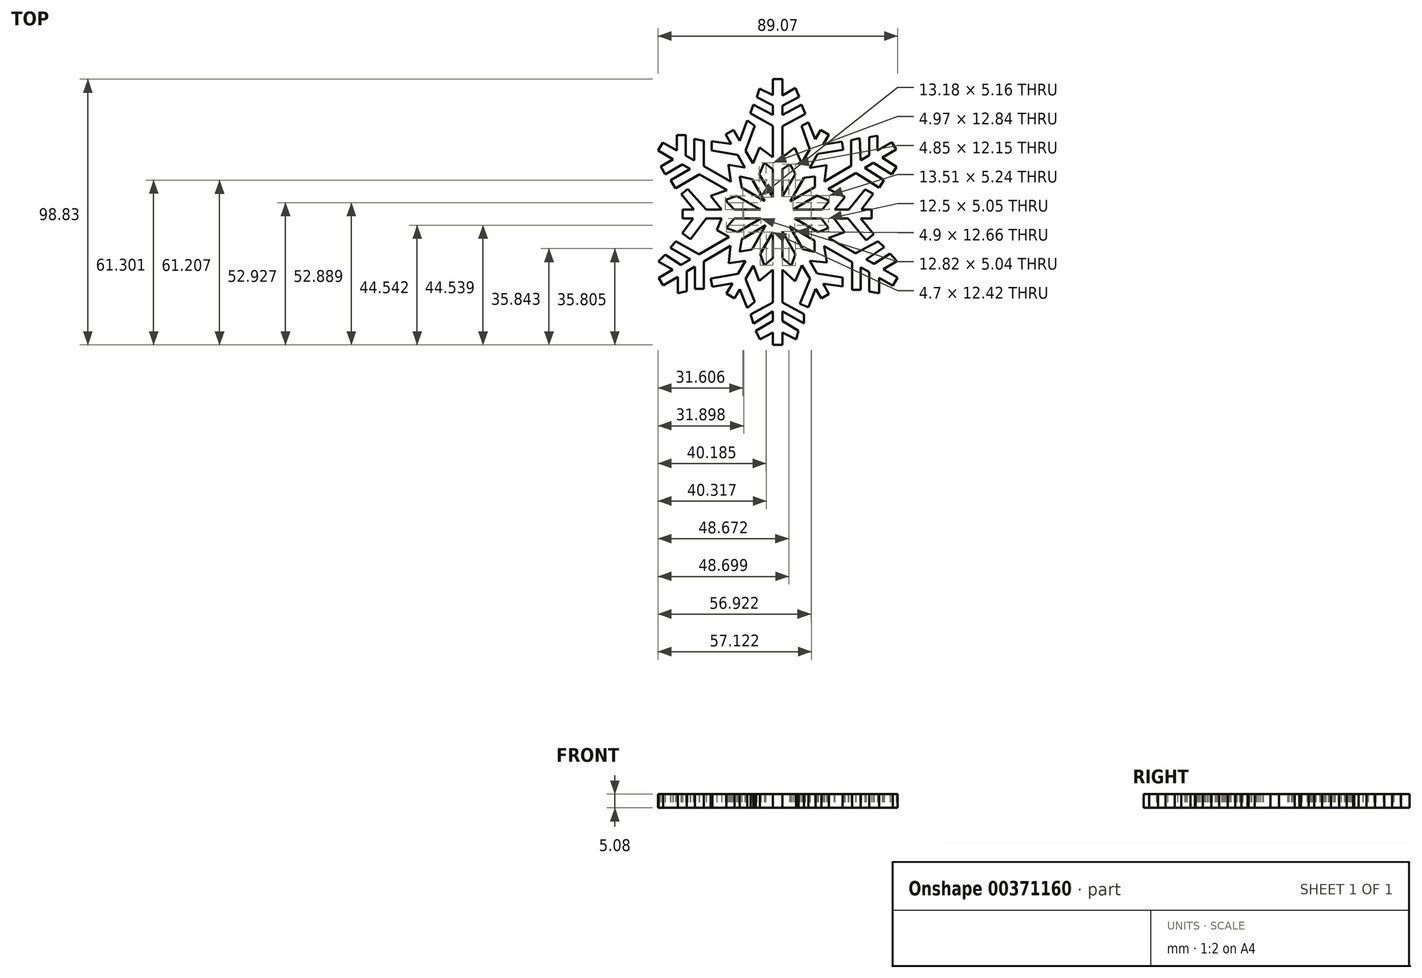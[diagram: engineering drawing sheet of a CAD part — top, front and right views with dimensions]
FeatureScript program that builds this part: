
annotation { "Feature Type Name" : "Feature", "Feature Type Description" : "" }
export const myFeature = defineFeature(function(context is Context, id is Id, definition is map)
    precondition{}
    {
        {
            var Q0;
            Q0=qCreatedBy(makeId("Top.planeOp"),FACE);
            var sketch = newSketch(context, id + "F0", { "sketchPlane" : qUnion([Q0])});
            skLineSegment(sketch, "E0.bottom", {"start": v(-35.17, -1.59) * mm, "end": v(35.1, -1.59) * mm});
            skLineSegment(sketch, "E0.top", {"start": v(-35.17, 1.66) * mm, "end": v(35.1, 1.66) * mm});
            skLineSegment(sketch, "E0.left", {"start": v(-35.17, -1.59) * mm, "end": v(-35.17, 1.66) * mm});
            skLineSegment(sketch, "E0.right", {"start": v(35.1, -1.59) * mm, "end": v(35.1, 1.66) * mm});
            skLineSegment(sketch, "E1", {"start": v(-19.17, 29.64) * mm, "end": v(-16.28, 31.23) * mm});
            skLineSegment(sketch, "E2", {"start": v(-16.28, 31.23) * mm, "end": v(19.17, -29.65) * mm});
            skLineSegment(sketch, "E3", {"start": v(19.17, -29.65) * mm, "end": v(16.32, -31.31) * mm});
            skLineSegment(sketch, "E4", {"start": v(16.32, -31.31) * mm, "end": v(-19.17, 29.64) * mm});
            skLineSegment(sketch, "E5", {"start": v(-42.5, 26.63) * mm, "end": v(-44.39, 23.66) * mm});
            skLineSegment(sketch, "E6", {"start": v(-44.39, 23.66) * mm, "end": v(42.93, -26.64) * mm});
            skLineSegment(sketch, "E7", {"start": v(42.93, -26.64) * mm, "end": v(44.68, -23.6) * mm});
            skLineSegment(sketch, "E8", {"start": v(44.68, -23.6) * mm, "end": v(-42.5, 26.63) * mm});
            skLineSegment(sketch, "E9", {"start": v(16.12, 31.24) * mm, "end": v(19.1, 29.52) * mm});
            skLineSegment(sketch, "E10", {"start": v(19.1, 29.52) * mm, "end": v(-15.92, -31.28) * mm});
            skLineSegment(sketch, "E11", {"start": v(-15.92, -31.28) * mm, "end": v(-18.9, -29.56) * mm});
            skLineSegment(sketch, "E12", {"start": v(-18.9, -29.56) * mm, "end": v(16.12, 31.24) * mm});
            skLineSegment(sketch, "E13", {"start": v(42.56, 26.73) * mm, "end": v(44.15, 24) * mm});
            skLineSegment(sketch, "E14", {"start": v(44.15, 24) * mm, "end": v(-42.48, -26.44) * mm});
            skLineSegment(sketch, "E15", {"start": v(-42.48, -26.44) * mm, "end": v(-44.07, -23.7) * mm});
            skLineSegment(sketch, "E16", {"start": v(-44.07, -23.7) * mm, "end": v(42.56, 26.73) * mm});
            skLineSegment(sketch, "E17", {"start": v(-7.62, 43.46) * mm, "end": v(-6.6, 46.62) * mm});
            skLineSegment(sketch, "E18", {"start": v(-10.07, 37.55) * mm, "end": v(-8.85, 40.7) * mm});
            skLineSegment(sketch, "E19", {"start": v(1.86, 44.07) * mm, "end": v(6.75, 46.93) * mm});
            skLineSegment(sketch, "E20", {"start": v(6.75, 46.93) * mm, "end": v(8.18, 43.67) * mm});
            skLineSegment(sketch, "E21", {"start": v(8.18, 43.67) * mm, "end": v(1.86, 40.34) * mm});
            skLineSegment(sketch, "E22", {"start": v(1.86, 36.85) * mm, "end": v(9, 40.7) * mm});
            skLineSegment(sketch, "E23", {"start": v(9, 40.7) * mm, "end": v(10.42, 37.24) * mm});
            skLineSegment(sketch, "E24", {"start": v(10.42, 37.24) * mm, "end": v(1.86, 32.7) * mm});
            skLineSegment(sketch, "E25", {"start": v(12.01, 24.1) * mm, "end": v(9.05, 32.76) * mm});
            skLineSegment(sketch, "E26", {"start": v(9.05, 32.76) * mm, "end": v(11.56, 34.1) * mm});
            skLineSegment(sketch, "E27", {"start": v(11.56, 34.1) * mm, "end": v(14.14, 27.8) * mm});
            skLineSegment(sketch, "E28", {"start": v(17, 25.85) * mm, "end": v(24, 26.9) * mm});
            skLineSegment(sketch, "E29", {"start": v(24, 26.9) * mm, "end": v(24.46, 23.86) * mm});
            skLineSegment(sketch, "E30", {"start": v(24.46, 23.86) * mm, "end": v(15.03, 22.43) * mm});
            skLineSegment(sketch, "E31", {"start": v(34.16, 21.85) * mm, "end": v(34.16, 28.6) * mm});
            skLineSegment(sketch, "E32", {"start": v(34.16, 28.6) * mm, "end": v(37.18, 29.12) * mm});
            skLineSegment(sketch, "E33", {"start": v(37.18, 29.12) * mm, "end": v(37.18, 23.6) * mm});
            skLineSegment(sketch, "E34", {"start": v(38.95, 20.98) * mm, "end": v(44.32, 17.6) * mm});
            skLineSegment(sketch, "E35", {"start": v(44.32, 17.6) * mm, "end": v(42.52, 14.74) * mm});
            skLineSegment(sketch, "E36", {"start": v(42.52, 14.74) * mm, "end": v(35.65, 19.05) * mm});
            skLineSegment(sketch, "E37", {"start": v(32.55, 17.25) * mm, "end": v(39.66, 12.67) * mm});
            skLineSegment(sketch, "E38", {"start": v(39.66, 12.67) * mm, "end": v(37.8, 9.8) * mm});
            skLineSegment(sketch, "E39", {"start": v(37.8, 9.8) * mm, "end": v(29.23, 15.32) * mm});
            skLineSegment(sketch, "E40", {"start": v(27.4, 17.91) * mm, "end": v(27.4, 27.47) * mm});
            skLineSegment(sketch, "E41", {"start": v(27.4, 27.47) * mm, "end": v(30.54, 28.26) * mm});
            skLineSegment(sketch, "E42", {"start": v(30.54, 28.26) * mm, "end": v(31, 20) * mm});
            skLineSegment(sketch, "E43", {"start": v(26.57, 1.66) * mm, "end": v(32.65, 9.23) * mm});
            skLineSegment(sketch, "E44", {"start": v(32.65, 9.23) * mm, "end": v(35.7, 7.51) * mm});
            skLineSegment(sketch, "E45", {"start": v(35.7, 7.51) * mm, "end": v(31.2, 1.66) * mm});
            skLineSegment(sketch, "E46", {"start": v(30.93, -1.59) * mm, "end": v(35.82, -7.43) * mm});
            skLineSegment(sketch, "E47", {"start": v(35.82, -7.43) * mm, "end": v(33.06, -9.74) * mm});
            skLineSegment(sketch, "E48", {"start": v(33.06, -9.74) * mm, "end": v(26.23, -1.59) * mm});
            skLineSegment(sketch, "E49", {"start": v(29.1, -14.62) * mm, "end": v(37.4, -10.07) * mm});
            skLineSegment(sketch, "E50", {"start": v(37.4, -10.07) * mm, "end": v(39.79, -12.32) * mm});
            skLineSegment(sketch, "E51", {"start": v(39.79, -12.32) * mm, "end": v(33.05, -16.9) * mm});
            skLineSegment(sketch, "E52", {"start": v(35.88, -18.52) * mm, "end": v(41.9, -14.7) * mm});
            skLineSegment(sketch, "E53", {"start": v(41.9, -14.7) * mm, "end": v(44.41, -17.47) * mm});
            skLineSegment(sketch, "E54", {"start": v(44.41, -17.47) * mm, "end": v(39.42, -20.56) * mm});
            skLineSegment(sketch, "E55", {"start": v(37.86, -23.72) * mm, "end": v(37.86, -29.37) * mm});
            skLineSegment(sketch, "E56", {"start": v(37.86, -29.37) * mm, "end": v(34.1, -28.84) * mm});
            skLineSegment(sketch, "E57", {"start": v(34.1, -28.84) * mm, "end": v(34.1, -21.56) * mm});
            skLineSegment(sketch, "E58", {"start": v(30.93, -19.73) * mm, "end": v(30.93, -28.18) * mm});
            skLineSegment(sketch, "E59", {"start": v(30.93, -28.18) * mm, "end": v(27.76, -28.18) * mm});
            skLineSegment(sketch, "E60", {"start": v(27.76, -28.18) * mm, "end": v(27.76, -17.9) * mm});
            skLineSegment(sketch, "E61", {"start": v(14.72, -22.01) * mm, "end": v(24.2, -23.55) * mm});
            skLineSegment(sketch, "E62", {"start": v(24.2, -23.55) * mm, "end": v(24.2, -26.86) * mm});
            skLineSegment(sketch, "E63", {"start": v(24.2, -26.86) * mm, "end": v(16.98, -25.9) * mm});
            skLineSegment(sketch, "E64", {"start": v(14.26, -27.79) * mm, "end": v(11.5, -34.65) * mm});
            skLineSegment(sketch, "E65", {"start": v(11.5, -34.65) * mm, "end": v(8.38, -33.4) * mm});
            skLineSegment(sketch, "E66", {"start": v(8.38, -33.4) * mm, "end": v(12.12, -24.1) * mm});
            skLineSegment(sketch, "E67", {"start": v(1.86, -32.89) * mm, "end": v(9.94, -37.17) * mm});
            skLineSegment(sketch, "E68", {"start": v(9.94, -37.17) * mm, "end": v(9.94, -40.6) * mm});
            skLineSegment(sketch, "E69", {"start": v(9.94, -40.6) * mm, "end": v(1.86, -36.14) * mm});
            skLineSegment(sketch, "E70", {"start": v(1.86, -39.74) * mm, "end": v(7.89, -43.34) * mm});
            skLineSegment(sketch, "E71", {"start": v(7.89, -43.34) * mm, "end": v(7.03, -46.6) * mm});
            skLineSegment(sketch, "E72", {"start": v(7.03, -46.6) * mm, "end": v(1.86, -44.03) * mm});
            skLineSegment(sketch, "E73", {"start": v(-8.06, -43.34) * mm, "end": v(-6.43, -46.56) * mm});
            skLineSegment(sketch, "E74", {"start": v(-9.94, -37.34) * mm, "end": v(-8.91, -40.77) * mm});
            skLineSegment(sketch, "E75", {"start": v(-11.77, -24.08) * mm, "end": v(-8.4, -32.54) * mm});
            skLineSegment(sketch, "E76", {"start": v(-8.4, -32.54) * mm, "end": v(-11.14, -34.94) * mm});
            skLineSegment(sketch, "E77", {"start": v(-11.14, -34.94) * mm, "end": v(-13.95, -27.85) * mm});
            skLineSegment(sketch, "E78", {"start": v(-16.68, -25.69) * mm, "end": v(-24.17, -27.06) * mm});
            skLineSegment(sketch, "E79", {"start": v(-24.17, -27.06) * mm, "end": v(-24.73, -24.01) * mm});
            skLineSegment(sketch, "E80", {"start": v(-24.73, -24.01) * mm, "end": v(-14.65, -22.17) * mm});
            skLineSegment(sketch, "E81", {"start": v(-27.35, -17.63) * mm, "end": v(-27.35, -27.74) * mm});
            skLineSegment(sketch, "E82", {"start": v(-27.35, -27.74) * mm, "end": v(-30.68, -27.74) * mm});
            skLineSegment(sketch, "E83", {"start": v(-30.68, -27.74) * mm, "end": v(-30.68, -19.57) * mm});
            skLineSegment(sketch, "E84", {"start": v(-33.66, -21.3) * mm, "end": v(-33.66, -28.6) * mm});
            skLineSegment(sketch, "E85", {"start": v(-33.66, -28.6) * mm, "end": v(-37.03, -29.46) * mm});
            skLineSegment(sketch, "E86", {"start": v(-37.03, -29.46) * mm, "end": v(-37.03, -23.26) * mm});
            skLineSegment(sketch, "E87", {"start": v(-38.9, -20.7) * mm, "end": v(-44.23, -17.63) * mm});
            skLineSegment(sketch, "E88", {"start": v(-44.23, -17.63) * mm, "end": v(-41.65, -15.06) * mm});
            skLineSegment(sketch, "E89", {"start": v(-41.65, -15.06) * mm, "end": v(-35.83, -18.9) * mm});
            skLineSegment(sketch, "E90", {"start": v(-39.77, -12.49) * mm, "end": v(-37.71, -10.09) * mm});
            skLineSegment(sketch, "E91", {"start": v(-37.71, -10.09) * mm, "end": v(-29.07, -14.97) * mm});
            skLineSegment(sketch, "E92", {"start": v(-26.4, -1.59) * mm, "end": v(-32.23, -9.4) * mm});
            skLineSegment(sketch, "E93", {"start": v(-32.23, -9.4) * mm, "end": v(-35.33, -7.09) * mm});
            skLineSegment(sketch, "E94", {"start": v(-35.33, -7.09) * mm, "end": v(-31.23, -1.59) * mm});
            skLineSegment(sketch, "E95", {"start": v(-31.03, 1.66) * mm, "end": v(-35.66, 7.4) * mm});
            skLineSegment(sketch, "E96", {"start": v(-35.66, 7.4) * mm, "end": v(-33.26, 9.33) * mm});
            skLineSegment(sketch, "E97", {"start": v(-33.26, 9.33) * mm, "end": v(-26.4, 1.66) * mm});
            skLineSegment(sketch, "E98", {"start": v(-28.94, 14.76) * mm, "end": v(-37.88, 9.62) * mm});
            skLineSegment(sketch, "E99", {"start": v(-37.88, 9.62) * mm, "end": v(-39.61, 12.63) * mm});
            skLineSegment(sketch, "E100", {"start": v(-39.61, 12.63) * mm, "end": v(-32.42, 16.77) * mm});
            skLineSegment(sketch, "E101", {"start": v(-35.34, 18.45) * mm, "end": v(-41.65, 14.77) * mm});
            skLineSegment(sketch, "E102", {"start": v(-41.65, 14.77) * mm, "end": v(-43.37, 17.7) * mm});
            skLineSegment(sketch, "E103", {"start": v(-43.37, 17.7) * mm, "end": v(-38.74, 20.4) * mm});
            skLineSegment(sketch, "E104", {"start": v(-37.3, 23.63) * mm, "end": v(-37.3, 29.34) * mm});
            skLineSegment(sketch, "E105", {"start": v(-37.3, 29.34) * mm, "end": v(-34.11, 29.34) * mm});
            skLineSegment(sketch, "E106", {"start": v(-34.11, 29.34) * mm, "end": v(-34.11, 21.8) * mm});
            skLineSegment(sketch, "E107", {"start": v(-30.85, 19.92) * mm, "end": v(-30.85, 27.97) * mm});
            skLineSegment(sketch, "E108", {"start": v(-30.85, 27.97) * mm, "end": v(-27.26, 27.28) * mm});
            skLineSegment(sketch, "E109", {"start": v(-27.26, 27.28) * mm, "end": v(-27.26, 17.85) * mm});
            skLineSegment(sketch, "E110", {"start": v(-14.73, 22.02) * mm, "end": v(-24.45, 23.66) * mm});
            skLineSegment(sketch, "E111", {"start": v(-24.45, 23.66) * mm, "end": v(-24.45, 27.1) * mm});
            skLineSegment(sketch, "E112", {"start": v(-24.45, 27.1) * mm, "end": v(-17.1, 26.08) * mm});
            skLineSegment(sketch, "E113", {"start": v(-13.93, 27.2) * mm, "end": v(-11.25, 34.8) * mm});
            skLineSegment(sketch, "E114", {"start": v(-11.25, 34.8) * mm, "end": v(-8.34, 32.75) * mm});
            skLineSegment(sketch, "E115", {"start": v(-8.34, 32.75) * mm, "end": v(-11.83, 23.6) * mm});
            skLineSegment(sketch, "E116", {"start": v(-9.03, 18.78) * mm, "end": v(-6.64, 24.78) * mm});
            skLineSegment(sketch, "E117", {"start": v(-6.69, 14.76) * mm, "end": v(-4.8, 19.07) * mm});
            skLineSegment(sketch, "E118", {"start": v(1.86, 21.11) * mm, "end": v(6.51, 24.68) * mm});
            skLineSegment(sketch, "E119", {"start": v(6.51, 24.68) * mm, "end": v(9.07, 19) * mm});
            skLineSegment(sketch, "E120", {"start": v(12.04, 17.24) * mm, "end": v(18.33, 18.16) * mm});
            skLineSegment(sketch, "E121", {"start": v(18.33, 18.16) * mm, "end": v(17.5, 12.14) * mm});
            skLineSegment(sketch, "E122", {"start": v(9.86, 13.47) * mm, "end": v(13.95, 13.98) * mm});
            skLineSegment(sketch, "E123", {"start": v(13.95, 13.98) * mm, "end": v(13.95, 10.08) * mm});
            skLineSegment(sketch, "E124", {"start": v(18.89, 9.3) * mm, "end": v(25.16, 6.43) * mm});
            skLineSegment(sketch, "E125", {"start": v(25.16, 6.43) * mm, "end": v(21.33, 1.66) * mm});
            skLineSegment(sketch, "E126", {"start": v(16.7, 1.66) * mm, "end": v(19.29, 4.94) * mm});
            skLineSegment(sketch, "E127", {"start": v(19.29, 4.94) * mm, "end": v(14.77, 6.9) * mm});
            skLineSegment(sketch, "E128", {"start": v(21.03, -1.59) * mm, "end": v(25.03, -6.64) * mm});
            skLineSegment(sketch, "E129", {"start": v(25.03, -6.64) * mm, "end": v(19, -8.8) * mm});
            skLineSegment(sketch, "E130", {"start": v(15.24, -6.64) * mm, "end": v(18.98, -5.22) * mm});
            skLineSegment(sketch, "E131", {"start": v(18.98, -5.22) * mm, "end": v(16.39, -1.59) * mm});
            skLineSegment(sketch, "E132", {"start": v(17.4, -11.94) * mm, "end": v(18.43, -17.96) * mm});
            skLineSegment(sketch, "E133", {"start": v(18.43, -17.96) * mm, "end": v(12.01, -17.36) * mm});
            skLineSegment(sketch, "E134", {"start": v(9.48, -13.01) * mm, "end": v(13.87, -14.1) * mm});
            skLineSegment(sketch, "E135", {"start": v(13.87, -14.1) * mm, "end": v(13.87, -9.9) * mm});
            skLineSegment(sketch, "E136", {"start": v(6.76, -14.9) * mm, "end": v(5.23, -19.13) * mm});
            skLineSegment(sketch, "E137", {"start": v(5.23, -19.13) * mm, "end": v(1.86, -16.3) * mm});
            skLineSegment(sketch, "E138", {"start": v(1.86, -20.7) * mm, "end": v(6.56, -25.03) * mm});
            skLineSegment(sketch, "E139", {"start": v(6.56, -25.03) * mm, "end": v(9.13, -18.98) * mm});
            skLineSegment(sketch, "E140", {"start": v(-4.83, -19.06) * mm, "end": v(-6.43, -14.8) * mm});
            skLineSegment(sketch, "E141", {"start": v(-8.89, -19.07) * mm, "end": v(-6.8, -24.8) * mm});
            skLineSegment(sketch, "E142", {"start": v(-11.86, -17.32) * mm, "end": v(-18.04, -18.27) * mm});
            skLineSegment(sketch, "E143", {"start": v(-18.04, -18.27) * mm, "end": v(-17.35, -11.8) * mm});
            skLineSegment(sketch, "E144", {"start": v(-13.23, -9.4) * mm, "end": v(-13.95, -13.95) * mm});
            skLineSegment(sketch, "E145", {"start": v(-13.95, -13.95) * mm, "end": v(-9.43, -13.1) * mm});
            skLineSegment(sketch, "E146", {"start": v(-14.74, -6.63) * mm, "end": v(-18.9, -5.22) * mm});
            skLineSegment(sketch, "E147", {"start": v(-18.9, -5.22) * mm, "end": v(-16, -1.59) * mm});
            skLineSegment(sketch, "E148", {"start": v(-16.07, 1.66) * mm, "end": v(-19.37, 5.3) * mm});
            skLineSegment(sketch, "E149", {"start": v(-19.37, 5.3) * mm, "end": v(-15.15, 6.82) * mm});
            skLineSegment(sketch, "E150", {"start": v(-18.73, 8.88) * mm, "end": v(-24.72, 6.72) * mm});
            skLineSegment(sketch, "E151", {"start": v(-24.72, 6.72) * mm, "end": v(-20.7, 1.66) * mm});
            skLineSegment(sketch, "E152", {"start": v(-13.25, 9.78) * mm, "end": v(-13.95, 13.95) * mm});
            skLineSegment(sketch, "E153", {"start": v(-13.95, 13.95) * mm, "end": v(-9.47, 12.98) * mm});
            skLineSegment(sketch, "E154", {"start": v(-12.02, 17.36) * mm, "end": v(-18.12, 18.28) * mm});
            skLineSegment(sketch, "E155", {"start": v(-18.12, 18.28) * mm, "end": v(-17.25, 12.09) * mm});
            skLineSegment(sketch, "E156", {"start": v(-39.77, -12.49) * mm, "end": v(-32.21, -16.8) * mm});
            skLineSegment(sketch, "E157", {"start": v(1.86, 50.18) * mm, "end": v(-1.72, 50.18) * mm});
            skLineSegment(sketch, "E158", {"start": v(-1.72, 50.18) * mm, "end": v(-1.72, -48.65) * mm});
            skLineSegment(sketch, "E159", {"start": v(-1.72, -48.65) * mm, "end": v(1.86, -48.65) * mm});
            skLineSegment(sketch, "E160", {"start": v(1.86, -48.65) * mm, "end": v(1.86, 50.18) * mm});
            skLineSegment(sketch, "E161", {"start": v(-6.6, 46.62) * mm, "end": v(-1.72, 44.29) * mm});
            skLineSegment(sketch, "E162", {"start": v(-7.62, 43.46) * mm, "end": v(-1.72, 40.5) * mm});
            skLineSegment(sketch, "E163", {"start": v(-8.85, 40.7) * mm, "end": v(-1.72, 36.85) * mm});
            skLineSegment(sketch, "E164", {"start": v(-10.07, 37.55) * mm, "end": v(-1.72, 32.83) * mm});
            skLineSegment(sketch, "E165", {"start": v(-6.64, 24.78) * mm, "end": v(-1.72, 21.11) * mm});
            skLineSegment(sketch, "E166", {"start": v(-4.8, 19.07) * mm, "end": v(-1.72, 16.68) * mm});
            skLineSegment(sketch, "E167", {"start": v(-4.83, -19.06) * mm, "end": v(-1.72, -16.3) * mm});
            skLineSegment(sketch, "E168", {"start": v(-6.8, -24.8) * mm, "end": v(-1.72, -20.7) * mm});
            skLineSegment(sketch, "E169", {"start": v(-9.94, -37.34) * mm, "end": v(-1.72, -32.89) * mm});
            skLineSegment(sketch, "E170", {"start": v(-8.91, -40.77) * mm, "end": v(-1.72, -36.14) * mm});
            skLineSegment(sketch, "E171", {"start": v(-8.06, -43.34) * mm, "end": v(-1.72, -39.74) * mm});
            skLineSegment(sketch, "E172", {"start": v(-6.43, -46.56) * mm, "end": v(-1.72, -44.03) * mm});
            skLineSegment(sketch, "E173", {"start": v(-20.7, -1.59) * mm, "end": v(-22.48, -5.93) * mm});
            skPoint(sketch, "E173.endSnap0", {"position": v(-16.82, -5.93) * mm});
            skLineSegment(sketch, "E174", {"start": v(-22.48, -5.93) * mm, "end": v(-17.94, -8.5) * mm});
            skLineSegment(sketch, "E175", {"start": v(1.86, 16.68) * mm, "end": v(4.72, 18.63) * mm});
            skLineSegment(sketch, "E176", {"start": v(4.72, 18.63) * mm, "end": v(6.7, 14.9) * mm});
            skSolve(sketch);
        }
        {
            var Q0;
            {var subQ13=sQuery(id+"F0.wireOp",EDGE,"E5");Q0=makeQuery(id+"F0.imprint","IMPRINT",FACE,{"disambiguationData":[TD([[makeQuery(id+"F0.imprint","IMPRINT",EDGE,{"derivedFrom":subQ13}),1.0]])]});}
            var Q1;
            {var subQ0=sQuery(id+"F0.wireOp",EDGE,"E104");Q1=makeQuery(id+"F0.imprint","IMPRINT",FACE,{"disambiguationData":[TD([[makeQuery(id+"F0.imprint","IMPRINT",EDGE,{"derivedFrom":subQ0}),-1.0]])]});}
            var Q2;
            {var subQ0=sQuery(id+"F0.wireOp",EDGE,"E101");Q2=makeQuery(id+"F0.imprint","IMPRINT",FACE,{"disambiguationData":[TD([[makeQuery(id+"F0.imprint","IMPRINT",EDGE,{"derivedFrom":subQ0}),-1.0]])]});}
            var Q3;
            {var subQ0=sQuery(id+"F0.wireOp",EDGE,"E98");Q3=makeQuery(id+"F0.imprint","IMPRINT",FACE,{"disambiguationData":[TD([[makeQuery(id+"F0.imprint","IMPRINT",EDGE,{"derivedFrom":subQ0}),-1.0]])]});}
            var Q4;
            {var subQ0=sQuery(id+"F0.wireOp",EDGE,"E107");Q4=makeQuery(id+"F0.imprint","IMPRINT",FACE,{"disambiguationData":[TD([[makeQuery(id+"F0.imprint","IMPRINT",EDGE,{"derivedFrom":subQ0}),-1.0]])]});}
            var Q5;
            {var subQ0=sQuery(id+"F0.wireOp",EDGE,"E110");Q5=makeQuery(id+"F0.imprint","IMPRINT",FACE,{"disambiguationData":[TD([[makeQuery(id+"F0.imprint","IMPRINT",EDGE,{"derivedFrom":subQ0}),-1.0]])]});}
            var Q6;
            {var subQ0=sQuery(id+"F0.wireOp",EDGE,"E113");Q6=makeQuery(id+"F0.imprint","IMPRINT",FACE,{"disambiguationData":[TD([[makeQuery(id+"F0.imprint","IMPRINT",EDGE,{"derivedFrom":subQ0}),-1.0]])]});}
            var Q7;
            {var subQ12=sQuery(id+"F0.wireOp",EDGE,"E1");Q7=makeQuery(id+"F0.imprint","IMPRINT",FACE,{"disambiguationData":[TD([[makeQuery(id+"F0.imprint","IMPRINT",EDGE,{"derivedFrom":subQ12}),-1.0]])]});}
            var Q8;
            {var subQ1=sQuery(id+"F0.wireOp",EDGE,"E152");Q8=makeQuery(id+"F0.imprint","IMPRINT",FACE,{"disambiguationData":[TD([[makeQuery(id+"F0.imprint","IMPRINT",EDGE,{"derivedFrom":subQ1}),1.0]])]});}
            var Q9;
            {var subQ0=sQuery(id+"F0.wireOp",EDGE,"E116");Q9=makeQuery(id+"F0.imprint","IMPRINT",FACE,{"disambiguationData":[TD([[makeQuery(id+"F0.imprint","IMPRINT",EDGE,{"derivedFrom":subQ0}),-1.0]])]});}
            var Q10;
            {var subQ0=sQuery(id+"F0.wireOp",EDGE,"KPcRYftw-hzLj-4d0o-mOsO-WIoxSP8k2R06");Q10=makeQuery(id+"F0.imprint","IMPRINT",FACE,{"disambiguationData":[TD([[makeQuery(id+"F0.imprint","IMPRINT",EDGE,{"derivedFrom":subQ0}),-1.0]])]});}
            var Q11;
            {var subQ0=sQuery(id+"F0.wireOp",EDGE,"7N0yXcb6-XQXa-j7w6-wTz8-wrRACawmk1rM");Q11=makeQuery(id+"F0.imprint","IMPRINT",FACE,{"disambiguationData":[TD([[makeQuery(id+"F0.imprint","IMPRINT",EDGE,{"derivedFrom":subQ0}),-1.0]])]});}
            var Q12;
            {var subQ14=sQuery(id+"F0.wireOp",EDGE,"6uGL5S95-GSbb-ZpDM-s1wd-MvVSDa6vKhNd.bottom");Q12=makeQuery(id+"F0.imprint","IMPRINT",FACE,{"disambiguationData":[TD([[makeQuery(id+"F0.imprint","IMPRINT",EDGE,{"derivedFrom":subQ14}),-1.0]])]});}
            var Q13;
            {var subQ0=sQuery(id+"F0.wireOp",EDGE,"E19");Q13=makeQuery(id+"F0.imprint","IMPRINT",FACE,{"disambiguationData":[TD([[makeQuery(id+"F0.imprint","IMPRINT",EDGE,{"derivedFrom":subQ0}),-1.0]])]});}
            var Q14;
            {var subQ0=sQuery(id+"F0.wireOp",EDGE,"E22");Q14=makeQuery(id+"F0.imprint","IMPRINT",FACE,{"disambiguationData":[TD([[makeQuery(id+"F0.imprint","IMPRINT",EDGE,{"derivedFrom":subQ0}),-1.0]])]});}
            var Q15;
            {var subQ0=sQuery(id+"F0.wireOp",EDGE,"E25");Q15=makeQuery(id+"F0.imprint","IMPRINT",FACE,{"disambiguationData":[TD([[makeQuery(id+"F0.imprint","IMPRINT",EDGE,{"derivedFrom":subQ0}),-1.0]])]});}
            var Q16;
            {var subQ0=sQuery(id+"F0.wireOp",EDGE,"E28");Q16=makeQuery(id+"F0.imprint","IMPRINT",FACE,{"disambiguationData":[TD([[makeQuery(id+"F0.imprint","IMPRINT",EDGE,{"derivedFrom":subQ0}),-1.0]])]});}
            var Q17;
            {var subQ13=sQuery(id+"F0.wireOp",EDGE,"E9");Q17=makeQuery(id+"F0.imprint","IMPRINT",FACE,{"disambiguationData":[TD([[makeQuery(id+"F0.imprint","IMPRINT",EDGE,{"derivedFrom":subQ13}),-1.0]])]});}
            var Q18;
            {var subQ4=sQuery(id+"F0.wireOp",EDGE,"V2TtZ5m8-MBKh-TBJa-3M3J-kMvBrJwQmeaq");Q18=makeQuery(id+"F0.imprint","IMPRINT",FACE,{"disambiguationData":[TD([[makeQuery(id+"F0.imprint","IMPRINT",EDGE,{"derivedFrom":subQ4}),1.0]])]});}
            var Q19;
            {var subQ0=sQuery(id+"F0.wireOp",EDGE,"E120");Q19=makeQuery(id+"F0.imprint","IMPRINT",FACE,{"disambiguationData":[TD([[makeQuery(id+"F0.imprint","IMPRINT",EDGE,{"derivedFrom":subQ0}),-1.0]])]});}
            var Q20;
            {var subQ13=sQuery(id+"F0.wireOp",EDGE,"E13");Q20=makeQuery(id+"F0.imprint","IMPRINT",FACE,{"disambiguationData":[TD([[makeQuery(id+"F0.imprint","IMPRINT",EDGE,{"derivedFrom":subQ13}),-1.0]])]});}
            var Q21;
            {var subQ0=sQuery(id+"F0.wireOp",EDGE,"E40");Q21=makeQuery(id+"F0.imprint","IMPRINT",FACE,{"disambiguationData":[TD([[makeQuery(id+"F0.imprint","IMPRINT",EDGE,{"derivedFrom":subQ0}),-1.0]])]});}
            var Q22;
            {var subQ0=sQuery(id+"F0.wireOp",EDGE,"E31");Q22=makeQuery(id+"F0.imprint","IMPRINT",FACE,{"disambiguationData":[TD([[makeQuery(id+"F0.imprint","IMPRINT",EDGE,{"derivedFrom":subQ0}),-1.0]])]});}
            var Q23;
            {var subQ0=sQuery(id+"F0.wireOp",EDGE,"E34");Q23=makeQuery(id+"F0.imprint","IMPRINT",FACE,{"disambiguationData":[TD([[makeQuery(id+"F0.imprint","IMPRINT",EDGE,{"derivedFrom":subQ0}),-1.0]])]});}
            var Q24;
            {var subQ0=sQuery(id+"F0.wireOp",EDGE,"E37");Q24=makeQuery(id+"F0.imprint","IMPRINT",FACE,{"disambiguationData":[TD([[makeQuery(id+"F0.imprint","IMPRINT",EDGE,{"derivedFrom":subQ0}),-1.0]])]});}
            var Q25;
            {var subQ1=sQuery(id+"F0.wireOp",EDGE,"E124");Q25=makeQuery(id+"F0.imprint","IMPRINT",FACE,{"disambiguationData":[TD([[makeQuery(id+"F0.imprint","IMPRINT",EDGE,{"derivedFrom":subQ1}),-1.0]])]});}
            var Q26;
            {var subQ6=sQuery(id+"F0.wireOp",EDGE,"E0.right");Q26=makeQuery(id+"F0.imprint","IMPRINT",FACE,{"disambiguationData":[TD([[makeQuery(id+"F0.imprint","IMPRINT",EDGE,{"derivedFrom":subQ6}),1.0]])]});}
            var Q27;
            {var subQ0=sQuery(id+"F0.wireOp",EDGE,"E43");Q27=makeQuery(id+"F0.imprint","IMPRINT",FACE,{"disambiguationData":[TD([[makeQuery(id+"F0.imprint","IMPRINT",EDGE,{"derivedFrom":subQ0}),-1.0]])]});}
            var Q28;
            {var subQ0=sQuery(id+"F0.wireOp",EDGE,"E46");Q28=makeQuery(id+"F0.imprint","IMPRINT",FACE,{"disambiguationData":[TD([[makeQuery(id+"F0.imprint","IMPRINT",EDGE,{"derivedFrom":subQ0}),-1.0]])]});}
            var Q29;
            {var subQ0=sQuery(id+"F0.wireOp",EDGE,"E128");Q29=makeQuery(id+"F0.imprint","IMPRINT",FACE,{"disambiguationData":[TD([[makeQuery(id+"F0.imprint","IMPRINT",EDGE,{"derivedFrom":subQ0}),-1.0]])]});}
            var Q30;
            {var subQ0=sQuery(id+"F0.wireOp",EDGE,"E7");Q30=makeQuery(id+"F0.imprint","IMPRINT",FACE,{"disambiguationData":[TD([[makeQuery(id+"F0.imprint","IMPRINT",EDGE,{"derivedFrom":subQ0}),1.0]])]});}
            var Q31;
            {var subQ0=sQuery(id+"F0.wireOp",EDGE,"E49");Q31=makeQuery(id+"F0.imprint","IMPRINT",FACE,{"disambiguationData":[TD([[makeQuery(id+"F0.imprint","IMPRINT",EDGE,{"derivedFrom":subQ0}),-1.0]])]});}
            var Q32;
            {var subQ0=sQuery(id+"F0.wireOp",EDGE,"E52");Q32=makeQuery(id+"F0.imprint","IMPRINT",FACE,{"disambiguationData":[TD([[makeQuery(id+"F0.imprint","IMPRINT",EDGE,{"derivedFrom":subQ0}),-1.0]])]});}
            var Q33;
            {var subQ0=sQuery(id+"F0.wireOp",EDGE,"E55");Q33=makeQuery(id+"F0.imprint","IMPRINT",FACE,{"disambiguationData":[TD([[makeQuery(id+"F0.imprint","IMPRINT",EDGE,{"derivedFrom":subQ0}),-1.0]])]});}
            var Q34;
            {var subQ0=sQuery(id+"F0.wireOp",EDGE,"E58");Q34=makeQuery(id+"F0.imprint","IMPRINT",FACE,{"disambiguationData":[TD([[makeQuery(id+"F0.imprint","IMPRINT",EDGE,{"derivedFrom":subQ0}),-1.0]])]});}
            var Q35;
            {var subQ1=sQuery(id+"F0.wireOp",EDGE,"E132");Q35=makeQuery(id+"F0.imprint","IMPRINT",FACE,{"disambiguationData":[TD([[makeQuery(id+"F0.imprint","IMPRINT",EDGE,{"derivedFrom":subQ1}),-1.0]])]});}
            var Q36;
            {var subQ0=sQuery(id+"F0.wireOp",EDGE,"E61");Q36=makeQuery(id+"F0.imprint","IMPRINT",FACE,{"disambiguationData":[TD([[makeQuery(id+"F0.imprint","IMPRINT",EDGE,{"derivedFrom":subQ0}),-1.0]])]});}
            var Q37;
            {var subQ0=sQuery(id+"F0.wireOp",EDGE,"E64");Q37=makeQuery(id+"F0.imprint","IMPRINT",FACE,{"disambiguationData":[TD([[makeQuery(id+"F0.imprint","IMPRINT",EDGE,{"derivedFrom":subQ0}),-1.0]])]});}
            var Q38;
            {var subQ4=sQuery(id+"F0.wireOp",EDGE,"E3");Q38=makeQuery(id+"F0.imprint","IMPRINT",FACE,{"disambiguationData":[TD([[makeQuery(id+"F0.imprint","IMPRINT",EDGE,{"derivedFrom":subQ4}),-1.0]])]});}
            var Q39;
            {var subQ1=sQuery(id+"F0.wireOp",EDGE,"E136");Q39=makeQuery(id+"F0.imprint","IMPRINT",FACE,{"disambiguationData":[TD([[makeQuery(id+"F0.imprint","IMPRINT",EDGE,{"derivedFrom":subQ1}),1.0]])]});}
            var Q40;
            {var subQ1=sQuery(id+"F0.wireOp",EDGE,"6uGL5S95-GSbb-ZpDM-s1wd-MvVSDa6vKhNd.top");Q40=makeQuery(id+"F0.imprint","IMPRINT",FACE,{"disambiguationData":[TD([[makeQuery(id+"F0.imprint","IMPRINT",EDGE,{"derivedFrom":subQ1}),1.0]])]});}
            var Q41;
            {var subQ0=sQuery(id+"F0.wireOp",EDGE,"E67");Q41=makeQuery(id+"F0.imprint","IMPRINT",FACE,{"disambiguationData":[TD([[makeQuery(id+"F0.imprint","IMPRINT",EDGE,{"derivedFrom":subQ0}),-1.0]])]});}
            var Q42;
            {var subQ0=sQuery(id+"F0.wireOp",EDGE,"E70");Q42=makeQuery(id+"F0.imprint","IMPRINT",FACE,{"disambiguationData":[TD([[makeQuery(id+"F0.imprint","IMPRINT",EDGE,{"derivedFrom":subQ0}),-1.0]])]});}
            var Q43;
            {var subQ0=sQuery(id+"F0.wireOp",EDGE,"AgjfrECO-wUj7-TZ4S-4cHH-89ThX9Ugsf9A");Q43=makeQuery(id+"F0.imprint","IMPRINT",FACE,{"disambiguationData":[TD([[makeQuery(id+"F0.imprint","IMPRINT",EDGE,{"derivedFrom":subQ0}),1.0]])]});}
            var Q44;
            {var subQ0=sQuery(id+"F0.wireOp",EDGE,"y6eyqB0O-g4zF-KDIH-16l5-euylJ0OMo6lk");Q44=makeQuery(id+"F0.imprint","IMPRINT",FACE,{"disambiguationData":[TD([[makeQuery(id+"F0.imprint","IMPRINT",EDGE,{"derivedFrom":subQ0}),1.0]])]});}
            var Q45;
            {var subQ3=sQuery(id+"F0.wireOp",EDGE,"PPsn6sRH-qw9p-LeI4-Ji2g-SvFjdvS5IeGd");Q45=makeQuery(id+"F0.imprint","IMPRINT",FACE,{"disambiguationData":[TD([[makeQuery(id+"F0.imprint","IMPRINT",EDGE,{"derivedFrom":subQ3}),1.0]])]});}
            var Q46;
            {var subQ0=sQuery(id+"F0.wireOp",EDGE,"E75");Q46=makeQuery(id+"F0.imprint","IMPRINT",FACE,{"disambiguationData":[TD([[makeQuery(id+"F0.imprint","IMPRINT",EDGE,{"derivedFrom":subQ0}),-1.0]])]});}
            var Q47;
            {var subQ0=sQuery(id+"F0.wireOp",EDGE,"E78");Q47=makeQuery(id+"F0.imprint","IMPRINT",FACE,{"disambiguationData":[TD([[makeQuery(id+"F0.imprint","IMPRINT",EDGE,{"derivedFrom":subQ0}),-1.0]])]});}
            var Q48;
            {var subQ0=sQuery(id+"F0.wireOp",EDGE,"E142");Q48=makeQuery(id+"F0.imprint","IMPRINT",FACE,{"disambiguationData":[TD([[makeQuery(id+"F0.imprint","IMPRINT",EDGE,{"derivedFrom":subQ0}),-1.0]])]});}
            var Q49;
            {var subQ0=sQuery(id+"F0.wireOp",EDGE,"E2");var subQ1=sQuery(id+"F0.wireOp",EDGE,"6uGL5S95-GSbb-ZpDM-s1wd-MvVSDa6vKhNd.left");var subQ2=makeQuery(id+"F0.imprint","INTERSECT",VERTEX,{"derivedFrom":[subQ1,subQ0]});Q49=makeQuery(id+"F0.imprint","IMPRINT",FACE,{"disambiguationData":[TD([[makeQuery(id+"F0.imprint","IMPRINT",EDGE,{"disambiguationData":[TD([[subQ2,-1.0]])],"derivedFrom":subQ1}),1.0]])]});}
            var Q50;
            {var subQ0=sQuery(id+"F0.wireOp",EDGE,"E8");var subQ1=sQuery(id+"F0.wireOp",EDGE,"6uGL5S95-GSbb-ZpDM-s1wd-MvVSDa6vKhNd.left");var subQ2=makeQuery(id+"F0.imprint","INTERSECT",VERTEX,{"derivedFrom":[subQ1,subQ0]});Q50=makeQuery(id+"F0.imprint","IMPRINT",FACE,{"disambiguationData":[TD([[makeQuery(id+"F0.imprint","IMPRINT",EDGE,{"disambiguationData":[TD([[subQ2,-1.0]])],"derivedFrom":subQ1}),-1.0]])]});}
            var Q51;
            {var subQ0=sQuery(id+"F0.wireOp",EDGE,"E6");var subQ1=sQuery(id+"F0.wireOp",EDGE,"E0.top");var subQ2=makeQuery(id+"F0.imprint","INTERSECT",VERTEX,{"derivedFrom":[subQ1,subQ0]});Q51=makeQuery(id+"F0.imprint","IMPRINT",FACE,{"disambiguationData":[TD([[makeQuery(id+"F0.imprint","IMPRINT",EDGE,{"disambiguationData":[TD([[subQ2,-1.0]])],"derivedFrom":subQ1}),-1.0]])]});}
            var Q52;
            {var subQ1=sQuery(id+"F0.wireOp",EDGE,"6uGL5S95-GSbb-ZpDM-s1wd-MvVSDa6vKhNd.left");var subQ7=sQuery(id+"F0.wireOp",EDGE,"E4");var subQ8=makeQuery(id+"F0.imprint","INTERSECT",VERTEX,{"derivedFrom":[subQ1,subQ7]});Q52=makeQuery(id+"F0.imprint","IMPRINT",FACE,{"disambiguationData":[TD([[makeQuery(id+"F0.imprint","IMPRINT",EDGE,{"disambiguationData":[TD([[subQ8,-1.0]])],"derivedFrom":subQ1}),-1.0]])]});}
            var Q53;
            {var subQ0=sQuery(id+"F0.wireOp",EDGE,"E0.top");var subQ1=sQuery(id+"F0.wireOp",EDGE,"6uGL5S95-GSbb-ZpDM-s1wd-MvVSDa6vKhNd.left");var subQ2=makeQuery(id+"F0.imprint","INTERSECT",VERTEX,{"derivedFrom":[subQ1,subQ0]});Q53=makeQuery(id+"F0.imprint","IMPRINT",FACE,{"disambiguationData":[TD([[makeQuery(id+"F0.imprint","IMPRINT",EDGE,{"disambiguationData":[TD([[subQ2,-1.0]])],"derivedFrom":subQ1}),-1.0]])]});}
            var Q54;
            {var subQ0=sQuery(id+"F0.wireOp",EDGE,"E16");var subQ1=sQuery(id+"F0.wireOp",EDGE,"6uGL5S95-GSbb-ZpDM-s1wd-MvVSDa6vKhNd.left");var subQ2=makeQuery(id+"F0.imprint","INTERSECT",VERTEX,{"derivedFrom":[subQ1,subQ0]});Q54=makeQuery(id+"F0.imprint","IMPRINT",FACE,{"disambiguationData":[TD([[makeQuery(id+"F0.imprint","IMPRINT",EDGE,{"disambiguationData":[TD([[subQ2,-1.0]])],"derivedFrom":subQ1}),-1.0]])]});}
            var Q55;
            {var subQ0=sQuery(id+"F0.wireOp",EDGE,"E16");var subQ1=sQuery(id+"F0.wireOp",EDGE,"6uGL5S95-GSbb-ZpDM-s1wd-MvVSDa6vKhNd.left");var subQ2=makeQuery(id+"F0.imprint","INTERSECT",VERTEX,{"derivedFrom":[subQ1,subQ0]});Q55=makeQuery(id+"F0.imprint","IMPRINT",FACE,{"disambiguationData":[TD([[makeQuery(id+"F0.imprint","IMPRINT",EDGE,{"disambiguationData":[TD([[subQ2,-1.0]])],"derivedFrom":subQ1}),1.0]])]});}
            var Q56;
            {var subQ0=sQuery(id+"F0.wireOp",EDGE,"E0.top");var subQ1=sQuery(id+"F0.wireOp",EDGE,"6uGL5S95-GSbb-ZpDM-s1wd-MvVSDa6vKhNd.left");var subQ2=makeQuery(id+"F0.imprint","INTERSECT",VERTEX,{"derivedFrom":[subQ1,subQ0]});Q56=makeQuery(id+"F0.imprint","IMPRINT",FACE,{"disambiguationData":[TD([[makeQuery(id+"F0.imprint","IMPRINT",EDGE,{"disambiguationData":[TD([[subQ2,-1.0]])],"derivedFrom":subQ1}),1.0]])]});}
            var Q57;
            {var subQ0=sQuery(id+"F0.wireOp",EDGE,"E8");var subQ1=sQuery(id+"F0.wireOp",EDGE,"6uGL5S95-GSbb-ZpDM-s1wd-MvVSDa6vKhNd.left");var subQ2=makeQuery(id+"F0.imprint","INTERSECT",VERTEX,{"derivedFrom":[subQ1,subQ0]});Q57=makeQuery(id+"F0.imprint","IMPRINT",FACE,{"disambiguationData":[TD([[makeQuery(id+"F0.imprint","IMPRINT",EDGE,{"disambiguationData":[TD([[subQ2,-1.0]])],"derivedFrom":subQ1}),1.0]])]});}
            var Q58;
            {var subQ0=sQuery(id+"F0.wireOp",EDGE,"E12");var subQ1=sQuery(id+"F0.wireOp",EDGE,"E0.top");var subQ2=makeQuery(id+"F0.imprint","INTERSECT",VERTEX,{"derivedFrom":[subQ1,subQ0]});Q58=makeQuery(id+"F0.imprint","IMPRINT",FACE,{"disambiguationData":[TD([[makeQuery(id+"F0.imprint","IMPRINT",EDGE,{"disambiguationData":[TD([[subQ2,-1.0]])],"derivedFrom":subQ1}),1.0]])]});}
            var Q59;
            {var subQ0=sQuery(id+"F0.wireOp",EDGE,"E12");var subQ1=sQuery(id+"F0.wireOp",EDGE,"E2");var subQ2=makeQuery(id+"F0.imprint","INTERSECT",VERTEX,{"derivedFrom":[subQ1,subQ0]});Q59=makeQuery(id+"F0.imprint","IMPRINT",FACE,{"disambiguationData":[TD([[makeQuery(id+"F0.imprint","IMPRINT",EDGE,{"disambiguationData":[TD([[subQ2,-1.0]])],"derivedFrom":subQ1}),-1.0]])]});}
            var Q60;
            {var subQ0=sQuery(id+"F0.wireOp",EDGE,"E16");var subQ1=sQuery(id+"F0.wireOp",EDGE,"E0.top");var subQ2=makeQuery(id+"F0.imprint","INTERSECT",VERTEX,{"derivedFrom":[subQ1,subQ0]});Q60=makeQuery(id+"F0.imprint","IMPRINT",FACE,{"disambiguationData":[TD([[makeQuery(id+"F0.imprint","IMPRINT",EDGE,{"disambiguationData":[TD([[subQ2,-1.0]])],"derivedFrom":subQ1}),1.0]])]});}
            var Q61;
            {var subQ0=sQuery(id+"F0.wireOp",EDGE,"E16");var subQ1=sQuery(id+"F0.wireOp",EDGE,"6uGL5S95-GSbb-ZpDM-s1wd-MvVSDa6vKhNd.right");var subQ2=makeQuery(id+"F0.imprint","INTERSECT",VERTEX,{"derivedFrom":[subQ1,subQ0]});Q61=makeQuery(id+"F0.imprint","IMPRINT",FACE,{"disambiguationData":[TD([[makeQuery(id+"F0.imprint","IMPRINT",EDGE,{"disambiguationData":[TD([[subQ2,-1.0]])],"derivedFrom":subQ1}),-1.0]])]});}
            var Q62;
            {var subQ0=sQuery(id+"F0.wireOp",EDGE,"E0.top");var subQ1=sQuery(id+"F0.wireOp",EDGE,"6uGL5S95-GSbb-ZpDM-s1wd-MvVSDa6vKhNd.right");var subQ2=makeQuery(id+"F0.imprint","INTERSECT",VERTEX,{"derivedFrom":[subQ1,subQ0]});Q62=makeQuery(id+"F0.imprint","IMPRINT",FACE,{"disambiguationData":[TD([[makeQuery(id+"F0.imprint","IMPRINT",EDGE,{"disambiguationData":[TD([[subQ2,-1.0]])],"derivedFrom":subQ1}),-1.0]])]});}
            var Q63;
            {var subQ0=sQuery(id+"F0.wireOp",EDGE,"E8");var subQ1=sQuery(id+"F0.wireOp",EDGE,"6uGL5S95-GSbb-ZpDM-s1wd-MvVSDa6vKhNd.right");var subQ2=makeQuery(id+"F0.imprint","INTERSECT",VERTEX,{"derivedFrom":[subQ1,subQ0]});Q63=makeQuery(id+"F0.imprint","IMPRINT",FACE,{"disambiguationData":[TD([[makeQuery(id+"F0.imprint","IMPRINT",EDGE,{"disambiguationData":[TD([[subQ2,-1.0]])],"derivedFrom":subQ1}),-1.0]])]});}
            var Q64;
            {var subQ0=sQuery(id+"F0.wireOp",EDGE,"E0.top");var subQ1=sQuery(id+"F0.wireOp",EDGE,"6uGL5S95-GSbb-ZpDM-s1wd-MvVSDa6vKhNd.right");var subQ2=makeQuery(id+"F0.imprint","INTERSECT",VERTEX,{"derivedFrom":[subQ1,subQ0]});Q64=makeQuery(id+"F0.imprint","IMPRINT",FACE,{"disambiguationData":[TD([[makeQuery(id+"F0.imprint","IMPRINT",EDGE,{"disambiguationData":[TD([[subQ2,-1.0]])],"derivedFrom":subQ1}),1.0]])]});}
            var Q65;
            {var subQ0=sQuery(id+"F0.wireOp",EDGE,"E8");var subQ1=sQuery(id+"F0.wireOp",EDGE,"6uGL5S95-GSbb-ZpDM-s1wd-MvVSDa6vKhNd.right");var subQ2=makeQuery(id+"F0.imprint","INTERSECT",VERTEX,{"derivedFrom":[subQ1,subQ0]});Q65=makeQuery(id+"F0.imprint","IMPRINT",FACE,{"disambiguationData":[TD([[makeQuery(id+"F0.imprint","IMPRINT",EDGE,{"disambiguationData":[TD([[subQ2,-1.0]])],"derivedFrom":subQ1}),1.0]])]});}
            var Q66;
            {var subQ0=sQuery(id+"F0.wireOp",EDGE,"E10");var subQ1=sQuery(id+"F0.wireOp",EDGE,"E2");var subQ2=makeQuery(id+"F0.imprint","INTERSECT",VERTEX,{"derivedFrom":[subQ1,subQ0]});Q66=makeQuery(id+"F0.imprint","IMPRINT",FACE,{"disambiguationData":[TD([[makeQuery(id+"F0.imprint","IMPRINT",EDGE,{"disambiguationData":[TD([[subQ2,-1.0]])],"derivedFrom":subQ1}),1.0]])]});}
            var Q67;
            {var subQ0=sQuery(id+"F0.wireOp",EDGE,"E10");var subQ1=sQuery(id+"F0.wireOp",EDGE,"E0.top");var subQ2=makeQuery(id+"F0.imprint","INTERSECT",VERTEX,{"derivedFrom":[subQ1,subQ0]});Q67=makeQuery(id+"F0.imprint","IMPRINT",FACE,{"disambiguationData":[TD([[makeQuery(id+"F0.imprint","IMPRINT",EDGE,{"disambiguationData":[TD([[subQ2,-1.0]])],"derivedFrom":subQ1}),-1.0]])]});}
            var Q68;
            {var subQ0=sQuery(id+"F0.wireOp",EDGE,"E2");var subQ1=sQuery(id+"F0.wireOp",EDGE,"E0.bottom");var subQ2=makeQuery(id+"F0.imprint","INTERSECT",VERTEX,{"derivedFrom":[subQ1,subQ0]});Q68=makeQuery(id+"F0.imprint","IMPRINT",FACE,{"disambiguationData":[TD([[makeQuery(id+"F0.imprint","IMPRINT",EDGE,{"disambiguationData":[TD([[subQ2,-1.0]])],"derivedFrom":subQ1}),1.0]])]});}
            var Q69;
            {var subQ0=sQuery(id+"F0.wireOp",EDGE,"E14");var subQ1=sQuery(id+"F0.wireOp",EDGE,"6uGL5S95-GSbb-ZpDM-s1wd-MvVSDa6vKhNd.right");var subQ2=makeQuery(id+"F0.imprint","INTERSECT",VERTEX,{"derivedFrom":[subQ1,subQ0]});Q69=makeQuery(id+"F0.imprint","IMPRINT",FACE,{"disambiguationData":[TD([[makeQuery(id+"F0.imprint","IMPRINT",EDGE,{"disambiguationData":[TD([[subQ2,-1.0]])],"derivedFrom":subQ1}),1.0]])]});}
            var Q70;
            {var subQ0=sQuery(id+"F0.wireOp",EDGE,"E0.bottom");var subQ1=sQuery(id+"F0.wireOp",EDGE,"6uGL5S95-GSbb-ZpDM-s1wd-MvVSDa6vKhNd.right");var subQ2=makeQuery(id+"F0.imprint","INTERSECT",VERTEX,{"derivedFrom":[subQ1,subQ0]});Q70=makeQuery(id+"F0.imprint","IMPRINT",FACE,{"disambiguationData":[TD([[makeQuery(id+"F0.imprint","IMPRINT",EDGE,{"disambiguationData":[TD([[subQ2,-1.0]])],"derivedFrom":subQ1}),1.0]])]});}
            var Q71;
            {var subQ0=sQuery(id+"F0.wireOp",EDGE,"E6");var subQ1=sQuery(id+"F0.wireOp",EDGE,"6uGL5S95-GSbb-ZpDM-s1wd-MvVSDa6vKhNd.right");var subQ2=makeQuery(id+"F0.imprint","INTERSECT",VERTEX,{"derivedFrom":[subQ1,subQ0]});Q71=makeQuery(id+"F0.imprint","IMPRINT",FACE,{"disambiguationData":[TD([[makeQuery(id+"F0.imprint","IMPRINT",EDGE,{"disambiguationData":[TD([[subQ2,-1.0]])],"derivedFrom":subQ1}),-1.0]])]});}
            var Q72;
            {var subQ0=sQuery(id+"F0.wireOp",EDGE,"E14");var subQ1=sQuery(id+"F0.wireOp",EDGE,"6uGL5S95-GSbb-ZpDM-s1wd-MvVSDa6vKhNd.left");var subQ2=makeQuery(id+"F0.imprint","INTERSECT",VERTEX,{"derivedFrom":[subQ1,subQ0]});Q72=makeQuery(id+"F0.imprint","IMPRINT",FACE,{"disambiguationData":[TD([[makeQuery(id+"F0.imprint","IMPRINT",EDGE,{"disambiguationData":[TD([[subQ2,-1.0]])],"derivedFrom":subQ1}),1.0]])]});}
            var Q73;
            {var subQ0=sQuery(id+"F0.wireOp",EDGE,"E15");Q73=makeQuery(id+"F0.imprint","IMPRINT",FACE,{"disambiguationData":[TD([[makeQuery(id+"F0.imprint","IMPRINT",EDGE,{"derivedFrom":subQ0}),-1.0]])]});}
            var Q74;
            {var subQ0=sQuery(id+"F0.wireOp",EDGE,"E6");var subQ1=sQuery(id+"F0.wireOp",EDGE,"6uGL5S95-GSbb-ZpDM-s1wd-MvVSDa6vKhNd.left");var subQ2=makeQuery(id+"F0.imprint","INTERSECT",VERTEX,{"derivedFrom":[subQ1,subQ0]});Q74=makeQuery(id+"F0.imprint","IMPRINT",FACE,{"disambiguationData":[TD([[makeQuery(id+"F0.imprint","IMPRINT",EDGE,{"disambiguationData":[TD([[subQ2,-1.0]])],"derivedFrom":subQ1}),-1.0]])]});}
            var Q75;
            {var subQ0=sQuery(id+"F0.wireOp",EDGE,"E6");var subQ1=sQuery(id+"F0.wireOp",EDGE,"6uGL5S95-GSbb-ZpDM-s1wd-MvVSDa6vKhNd.left");var subQ2=makeQuery(id+"F0.imprint","INTERSECT",VERTEX,{"derivedFrom":[subQ1,subQ0]});Q75=makeQuery(id+"F0.imprint","IMPRINT",FACE,{"disambiguationData":[TD([[makeQuery(id+"F0.imprint","IMPRINT",EDGE,{"disambiguationData":[TD([[subQ2,-1.0]])],"derivedFrom":subQ1}),1.0]])]});}
            var Q76;
            {var subQ0=sQuery(id+"F0.wireOp",EDGE,"E0.bottom");var subQ1=sQuery(id+"F0.wireOp",EDGE,"6uGL5S95-GSbb-ZpDM-s1wd-MvVSDa6vKhNd.left");var subQ2=makeQuery(id+"F0.imprint","INTERSECT",VERTEX,{"derivedFrom":[subQ1,subQ0]});Q76=makeQuery(id+"F0.imprint","IMPRINT",FACE,{"disambiguationData":[TD([[makeQuery(id+"F0.imprint","IMPRINT",EDGE,{"disambiguationData":[TD([[subQ2,-1.0]])],"derivedFrom":subQ1}),1.0]])]});}
            var Q77;
            {var subQ0=sQuery(id+"F0.wireOp",EDGE,"E10");var subQ1=sQuery(id+"F0.wireOp",EDGE,"E4");var subQ2=makeQuery(id+"F0.imprint","INTERSECT",VERTEX,{"derivedFrom":[subQ1,subQ0]});Q77=makeQuery(id+"F0.imprint","IMPRINT",FACE,{"disambiguationData":[TD([[makeQuery(id+"F0.imprint","IMPRINT",EDGE,{"disambiguationData":[TD([[subQ2,-1.0]])],"derivedFrom":subQ1}),-1.0]])]});}
            var Q78;
            {var subQ0=sQuery(id+"F0.wireOp",EDGE,"E0.bottom");var subQ1=sQuery(id+"F0.wireOp",EDGE,"6uGL5S95-GSbb-ZpDM-s1wd-MvVSDa6vKhNd.right");var subQ2=makeQuery(id+"F0.imprint","INTERSECT",VERTEX,{"derivedFrom":[subQ1,subQ0]});Q78=makeQuery(id+"F0.imprint","IMPRINT",FACE,{"disambiguationData":[TD([[makeQuery(id+"F0.imprint","IMPRINT",EDGE,{"disambiguationData":[TD([[subQ2,-1.0]])],"derivedFrom":subQ1}),-1.0]])]});}
            var Q79;
            {var subQ0=sQuery(id+"F0.wireOp",EDGE,"E14");var subQ1=sQuery(id+"F0.wireOp",EDGE,"E0.bottom");var subQ2=makeQuery(id+"F0.imprint","INTERSECT",VERTEX,{"derivedFrom":[subQ1,subQ0]});Q79=makeQuery(id+"F0.imprint","IMPRINT",FACE,{"disambiguationData":[TD([[makeQuery(id+"F0.imprint","IMPRINT",EDGE,{"disambiguationData":[TD([[subQ2,-1.0]])],"derivedFrom":subQ1}),-1.0]])]});}
            var Q80;
            {var subQ0=sQuery(id+"F0.wireOp",EDGE,"E14");var subQ1=sQuery(id+"F0.wireOp",EDGE,"E0.bottom");var subQ2=makeQuery(id+"F0.imprint","INTERSECT",VERTEX,{"derivedFrom":[subQ1,subQ0]});Q80=makeQuery(id+"F0.imprint","IMPRINT",FACE,{"disambiguationData":[TD([[makeQuery(id+"F0.imprint","IMPRINT",EDGE,{"disambiguationData":[TD([[subQ2,-1.0]])],"derivedFrom":subQ1}),1.0]])]});}
            var Q81;
            {var subQ0=sQuery(id+"F0.wireOp",EDGE,"E14");var subQ1=sQuery(id+"F0.wireOp",EDGE,"6uGL5S95-GSbb-ZpDM-s1wd-MvVSDa6vKhNd.right");var subQ2=makeQuery(id+"F0.imprint","INTERSECT",VERTEX,{"derivedFrom":[subQ1,subQ0]});Q81=makeQuery(id+"F0.imprint","IMPRINT",FACE,{"disambiguationData":[TD([[makeQuery(id+"F0.imprint","IMPRINT",EDGE,{"disambiguationData":[TD([[subQ2,-1.0]])],"derivedFrom":subQ1}),-1.0]])]});}
            var Q82;
            {var subQ0=sQuery(id+"F0.wireOp",EDGE,"E10");var subQ1=sQuery(id+"F0.wireOp",EDGE,"6uGL5S95-GSbb-ZpDM-s1wd-MvVSDa6vKhNd.right");var subQ2=makeQuery(id+"F0.imprint","INTERSECT",VERTEX,{"derivedFrom":[subQ1,subQ0]});Q82=makeQuery(id+"F0.imprint","IMPRINT",FACE,{"disambiguationData":[TD([[makeQuery(id+"F0.imprint","IMPRINT",EDGE,{"disambiguationData":[TD([[subQ2,-1.0]])],"derivedFrom":subQ1}),1.0]])]});}
            var Q83;
            {var subQ0=sQuery(id+"F0.wireOp",EDGE,"E2");var subQ1=sQuery(id+"F0.wireOp",EDGE,"6uGL5S95-GSbb-ZpDM-s1wd-MvVSDa6vKhNd.right");var subQ2=makeQuery(id+"F0.imprint","INTERSECT",VERTEX,{"derivedFrom":[subQ1,subQ0]});Q83=makeQuery(id+"F0.imprint","IMPRINT",FACE,{"disambiguationData":[TD([[makeQuery(id+"F0.imprint","IMPRINT",EDGE,{"disambiguationData":[TD([[subQ2,-1.0]])],"derivedFrom":subQ1}),1.0]])]});}
            var Q84;
            {var subQ0=sQuery(id+"F0.wireOp",EDGE,"E10");var subQ1=sQuery(id+"F0.wireOp",EDGE,"6uGL5S95-GSbb-ZpDM-s1wd-MvVSDa6vKhNd.right");var subQ2=makeQuery(id+"F0.imprint","INTERSECT",VERTEX,{"derivedFrom":[subQ1,subQ0]});Q84=makeQuery(id+"F0.imprint","IMPRINT",FACE,{"disambiguationData":[TD([[makeQuery(id+"F0.imprint","IMPRINT",EDGE,{"disambiguationData":[TD([[subQ2,-1.0]])],"derivedFrom":subQ1}),-1.0]])]});}
            var Q85;
            {var subQ15=sQuery(id+"F0.wireOp",EDGE,"6uGL5S95-GSbb-ZpDM-s1wd-MvVSDa6vKhNd.right");var subQ19=sQuery(id+"F0.wireOp",EDGE,"E2");var subQ21=makeQuery(id+"F0.imprint","INTERSECT",VERTEX,{"derivedFrom":[subQ15,subQ19]});Q85=makeQuery(id+"F0.imprint","IMPRINT",FACE,{"disambiguationData":[TD([[makeQuery(id+"F0.imprint","IMPRINT",EDGE,{"disambiguationData":[TD([[subQ21,-1.0]])],"derivedFrom":subQ15}),-1.0]])]});}
            var Q86;
            {var subQ0=sQuery(id+"F0.wireOp",EDGE,"E4");var subQ1=sQuery(id+"F0.wireOp",EDGE,"E0.bottom");var subQ2=makeQuery(id+"F0.imprint","INTERSECT",VERTEX,{"derivedFrom":[subQ1,subQ0]});Q86=makeQuery(id+"F0.imprint","IMPRINT",FACE,{"disambiguationData":[TD([[makeQuery(id+"F0.imprint","IMPRINT",EDGE,{"disambiguationData":[TD([[subQ2,-1.0]])],"derivedFrom":subQ1}),-1.0]])]});}
            var Q87;
            {var subQ0=sQuery(id+"F0.wireOp",EDGE,"E4");var subQ1=sQuery(id+"F0.wireOp",EDGE,"E0.bottom");var subQ2=makeQuery(id+"F0.imprint","INTERSECT",VERTEX,{"derivedFrom":[subQ1,subQ0]});Q87=makeQuery(id+"F0.imprint","IMPRINT",FACE,{"disambiguationData":[TD([[makeQuery(id+"F0.imprint","IMPRINT",EDGE,{"disambiguationData":[TD([[subQ2,-1.0]])],"derivedFrom":subQ1}),1.0]])]});}
            var Q88;
            {var subQ0=sQuery(id+"F0.wireOp",EDGE,"E6");var subQ1=sQuery(id+"F0.wireOp",EDGE,"E0.bottom");var subQ2=makeQuery(id+"F0.imprint","INTERSECT",VERTEX,{"derivedFrom":[subQ1,subQ0]});Q88=makeQuery(id+"F0.imprint","IMPRINT",FACE,{"disambiguationData":[TD([[makeQuery(id+"F0.imprint","IMPRINT",EDGE,{"disambiguationData":[TD([[subQ2,-1.0]])],"derivedFrom":subQ1}),-1.0]])]});}
            var Q89;
            {var subQ0=sQuery(id+"F0.wireOp",EDGE,"E12");var subQ1=sQuery(id+"F0.wireOp",EDGE,"6uGL5S95-GSbb-ZpDM-s1wd-MvVSDa6vKhNd.left");var subQ2=makeQuery(id+"F0.imprint","INTERSECT",VERTEX,{"derivedFrom":[subQ1,subQ0]});Q89=makeQuery(id+"F0.imprint","IMPRINT",FACE,{"disambiguationData":[TD([[makeQuery(id+"F0.imprint","IMPRINT",EDGE,{"disambiguationData":[TD([[subQ2,-1.0]])],"derivedFrom":subQ1}),1.0]])]});}
            var Q90;
            {var subQ0=sQuery(id+"F0.wireOp",EDGE,"E12");var subQ1=sQuery(id+"F0.wireOp",EDGE,"6uGL5S95-GSbb-ZpDM-s1wd-MvVSDa6vKhNd.left");var subQ2=makeQuery(id+"F0.imprint","INTERSECT",VERTEX,{"derivedFrom":[subQ1,subQ0]});Q90=makeQuery(id+"F0.imprint","IMPRINT",FACE,{"disambiguationData":[TD([[makeQuery(id+"F0.imprint","IMPRINT",EDGE,{"disambiguationData":[TD([[subQ2,-1.0]])],"derivedFrom":subQ1}),-1.0]])]});}
            var Q91;
            {var subQ0=sQuery(id+"F0.wireOp",EDGE,"E4");var subQ1=sQuery(id+"F0.wireOp",EDGE,"6uGL5S95-GSbb-ZpDM-s1wd-MvVSDa6vKhNd.left");var subQ2=makeQuery(id+"F0.imprint","INTERSECT",VERTEX,{"derivedFrom":[subQ1,subQ0]});Q91=makeQuery(id+"F0.imprint","IMPRINT",FACE,{"disambiguationData":[TD([[makeQuery(id+"F0.imprint","IMPRINT",EDGE,{"disambiguationData":[TD([[subQ2,-1.0]])],"derivedFrom":subQ1}),1.0]])]});}
            var Q92;
            {var subQ0=sQuery(id+"F0.wireOp",EDGE,"E8");var subQ1=sQuery(id+"F0.wireOp",EDGE,"E0.top");var subQ2=makeQuery(id+"F0.imprint","INTERSECT",VERTEX,{"derivedFrom":[subQ1,subQ0]});Q92=makeQuery(id+"F0.imprint","IMPRINT",FACE,{"disambiguationData":[TD([[makeQuery(id+"F0.imprint","IMPRINT",EDGE,{"disambiguationData":[TD([[subQ2,-1.0]])],"derivedFrom":subQ1}),1.0]])]});}
            var Q93;
            {var subQ0=sQuery(id+"F0.wireOp",EDGE,"E12");var subQ1=sQuery(id+"F0.wireOp",EDGE,"E0.top");var subQ2=makeQuery(id+"F0.imprint","INTERSECT",VERTEX,{"derivedFrom":[subQ1,subQ0]});Q93=makeQuery(id+"F0.imprint","IMPRINT",FACE,{"disambiguationData":[TD([[makeQuery(id+"F0.imprint","IMPRINT",EDGE,{"disambiguationData":[TD([[subQ2,-1.0]])],"derivedFrom":subQ1}),-1.0]])]});}
            var Q94;
            {var subQ0=sQuery(id+"F0.wireOp",EDGE,"E8");var subQ1=sQuery(id+"F0.wireOp",EDGE,"E0.top");var subQ2=makeQuery(id+"F0.imprint","INTERSECT",VERTEX,{"derivedFrom":[subQ1,subQ0]});Q94=makeQuery(id+"F0.imprint","IMPRINT",FACE,{"disambiguationData":[TD([[makeQuery(id+"F0.imprint","IMPRINT",EDGE,{"disambiguationData":[TD([[subQ2,-1.0]])],"derivedFrom":subQ1}),-1.0]])]});}
            var Q95;
            {var subQ0=sQuery(id+"F0.wireOp",EDGE,"E16");var subQ1=sQuery(id+"F0.wireOp",EDGE,"E0.bottom");var subQ2=makeQuery(id+"F0.imprint","INTERSECT",VERTEX,{"derivedFrom":[subQ1,subQ0]});Q95=makeQuery(id+"F0.imprint","IMPRINT",FACE,{"disambiguationData":[TD([[makeQuery(id+"F0.imprint","IMPRINT",EDGE,{"disambiguationData":[TD([[subQ2,-1.0]])],"derivedFrom":subQ1}),1.0]])]});}
            var Q96;
            {var subQ0=sQuery(id+"F0.wireOp",EDGE,"E12");var subQ1=sQuery(id+"F0.wireOp",EDGE,"6uGL5S95-GSbb-ZpDM-s1wd-MvVSDa6vKhNd.right");var subQ2=makeQuery(id+"F0.imprint","INTERSECT",VERTEX,{"derivedFrom":[subQ1,subQ0]});Q96=makeQuery(id+"F0.imprint","IMPRINT",FACE,{"disambiguationData":[TD([[makeQuery(id+"F0.imprint","IMPRINT",EDGE,{"disambiguationData":[TD([[subQ2,-1.0]])],"derivedFrom":subQ1}),-1.0]])]});}
            var Q97;
            {var subQ0=sQuery(id+"F0.wireOp",EDGE,"E16");var subQ1=sQuery(id+"F0.wireOp",EDGE,"6uGL5S95-GSbb-ZpDM-s1wd-MvVSDa6vKhNd.right");var subQ2=makeQuery(id+"F0.imprint","INTERSECT",VERTEX,{"derivedFrom":[subQ1,subQ0]});Q97=makeQuery(id+"F0.imprint","IMPRINT",FACE,{"disambiguationData":[TD([[makeQuery(id+"F0.imprint","IMPRINT",EDGE,{"disambiguationData":[TD([[subQ2,-1.0]])],"derivedFrom":subQ1}),1.0]])]});}
            var Q98;
            {var subQ4=sQuery(id+"F0.wireOp",EDGE,"E11");Q98=makeQuery(id+"F0.imprint","IMPRINT",FACE,{"disambiguationData":[TD([[makeQuery(id+"F0.imprint","IMPRINT",EDGE,{"derivedFrom":subQ4}),-1.0]])]});}
            var Q99;
            {var subQ0=sQuery(id+"F0.wireOp",EDGE,"E0.bottom");var subQ1=sQuery(id+"F0.wireOp",EDGE,"6uGL5S95-GSbb-ZpDM-s1wd-MvVSDa6vKhNd.left");var subQ2=makeQuery(id+"F0.imprint","INTERSECT",VERTEX,{"derivedFrom":[subQ1,subQ0]});Q99=makeQuery(id+"F0.imprint","IMPRINT",FACE,{"disambiguationData":[TD([[makeQuery(id+"F0.imprint","IMPRINT",EDGE,{"disambiguationData":[TD([[subQ2,-1.0]])],"derivedFrom":subQ1}),-1.0]])]});}
            var Q100;
            {var subQ0=sQuery(id+"F0.wireOp",EDGE,"E81");Q100=makeQuery(id+"F0.imprint","IMPRINT",FACE,{"disambiguationData":[TD([[makeQuery(id+"F0.imprint","IMPRINT",EDGE,{"derivedFrom":subQ0}),-1.0]])]});}
            var Q101;
            {var subQ0=sQuery(id+"F0.wireOp",EDGE,"E84");Q101=makeQuery(id+"F0.imprint","IMPRINT",FACE,{"disambiguationData":[TD([[makeQuery(id+"F0.imprint","IMPRINT",EDGE,{"derivedFrom":subQ0}),-1.0]])]});}
            var Q102;
            {var subQ0=sQuery(id+"F0.wireOp",EDGE,"E87");Q102=makeQuery(id+"F0.imprint","IMPRINT",FACE,{"disambiguationData":[TD([[makeQuery(id+"F0.imprint","IMPRINT",EDGE,{"derivedFrom":subQ0}),-1.0]])]});}
            var Q103;
            Q103=makeQuery(id+"F0.imprint","IMPRINT",FACE,{"disambiguationData":[TD([[makeQuery(id+"F0.imprint","IMPRINT",EDGE,{"derivedFrom":sQuery(id+"F0.wireOp",EDGE,"E90")}),-1.0]])]});
            var Q104;
            {var subQ0=sQuery(id+"F0.wireOp",EDGE,"E92");Q104=makeQuery(id+"F0.imprint","IMPRINT",FACE,{"disambiguationData":[TD([[makeQuery(id+"F0.imprint","IMPRINT",EDGE,{"derivedFrom":subQ0}),-1.0]])]});}
            var Q105;
            {var subQ4=sQuery(id+"F0.wireOp",EDGE,"E0.left");Q105=makeQuery(id+"F0.imprint","IMPRINT",FACE,{"disambiguationData":[TD([[makeQuery(id+"F0.imprint","IMPRINT",EDGE,{"derivedFrom":subQ4}),-1.0]])]});}
            var Q106;
            {var subQ0=sQuery(id+"F0.wireOp",EDGE,"E95");Q106=makeQuery(id+"F0.imprint","IMPRINT",FACE,{"disambiguationData":[TD([[makeQuery(id+"F0.imprint","IMPRINT",EDGE,{"derivedFrom":subQ0}),-1.0]])]});}
            var Q107;
            {var subQ1=sQuery(id+"F0.wireOp",EDGE,"E148");Q107=makeQuery(id+"F0.imprint","IMPRINT",FACE,{"disambiguationData":[TD([[makeQuery(id+"F0.imprint","IMPRINT",EDGE,{"derivedFrom":subQ1}),1.0]])]});}
            var Q108;
            {var subQ1=sQuery(id+"F0.wireOp",EDGE,"Bk4zX008-tbT7-cMU9-Ud3n-Ha9OmqY1tnYL");Q108=makeQuery(id+"F0.imprint","IMPRINT",FACE,{"disambiguationData":[TD([[makeQuery(id+"F0.imprint","IMPRINT",EDGE,{"derivedFrom":subQ1}),-1.0]])]});}
            var Q109;
            {var subQ11=sQuery(id+"F0.wireOp",EDGE,"E157");Q109=makeQuery(id+"F0.imprint","IMPRINT",FACE,{"disambiguationData":[TD([[makeQuery(id+"F0.imprint","IMPRINT",EDGE,{"derivedFrom":subQ11}),1.0]])]});}
            var Q110;
            Q110=makeQuery(id+"F0.imprint","IMPRINT",FACE,{"disambiguationData":[TD([[makeQuery(id+"F0.imprint","IMPRINT",EDGE,{"derivedFrom":sQuery(id+"F0.wireOp",EDGE,"E17")}),-1.0]])]});
            var Q111;
            Q111=makeQuery(id+"F0.imprint","IMPRINT",FACE,{"disambiguationData":[TD([[makeQuery(id+"F0.imprint","IMPRINT",EDGE,{"derivedFrom":sQuery(id+"F0.wireOp",EDGE,"E18")}),-1.0]])]});
            var Q112;
            {var subQ4=sQuery(id+"F0.wireOp",EDGE,"E140");Q112=makeQuery(id+"F0.imprint","IMPRINT",FACE,{"disambiguationData":[TD([[makeQuery(id+"F0.imprint","IMPRINT",EDGE,{"derivedFrom":subQ4}),1.0]])]});}
            var Q113;
            Q113=makeQuery(id+"F0.imprint","IMPRINT",FACE,{"disambiguationData":[TD([[makeQuery(id+"F0.imprint","IMPRINT",EDGE,{"derivedFrom":sQuery(id+"F0.wireOp",EDGE,"E74")}),1.0]])]});
            var Q114;
            {var subQ0=sQuery(id+"F0.wireOp",EDGE,"E159");Q114=makeQuery(id+"F0.imprint","IMPRINT",FACE,{"disambiguationData":[TD([[makeQuery(id+"F0.imprint","IMPRINT",EDGE,{"derivedFrom":subQ0}),1.0]])]});}
            var Q115;
            {var subQ0=sQuery(id+"F0.wireOp",EDGE,"E12");var subQ1=sQuery(id+"F0.wireOp",EDGE,"E2");var subQ2=makeQuery(id+"F0.imprint","INTERSECT",VERTEX,{"derivedFrom":[subQ1,subQ0]});Q115=makeQuery(id+"F0.imprint","IMPRINT",FACE,{"disambiguationData":[TD([[makeQuery(id+"F0.imprint","IMPRINT",EDGE,{"disambiguationData":[TD([[subQ2,-1.0]])],"derivedFrom":subQ1}),1.0]])]});}
            var Q116;
            {var subQ0=sQuery(id+"F0.wireOp",EDGE,"E158");var subQ1=sQuery(id+"F0.wireOp",EDGE,"E2");var subQ2=makeQuery(id+"F0.imprint","INTERSECT",VERTEX,{"derivedFrom":[subQ1,subQ0]});Q116=makeQuery(id+"F0.imprint","IMPRINT",FACE,{"disambiguationData":[TD([[makeQuery(id+"F0.imprint","IMPRINT",EDGE,{"disambiguationData":[TD([[subQ2,-1.0]])],"derivedFrom":subQ1}),-1.0]])]});}
            var Q117;
            {var subQ0=sQuery(id+"F0.wireOp",EDGE,"E4");var subQ1=sQuery(id+"F0.wireOp",EDGE,"E0.top");var subQ2=makeQuery(id+"F0.imprint","INTERSECT",VERTEX,{"derivedFrom":[subQ1,subQ0]});Q117=makeQuery(id+"F0.imprint","IMPRINT",FACE,{"disambiguationData":[TD([[makeQuery(id+"F0.imprint","IMPRINT",EDGE,{"disambiguationData":[TD([[subQ2,-1.0]])],"derivedFrom":subQ1}),1.0]])]});}
            var Q118;
            {var subQ0=sQuery(id+"F0.wireOp",EDGE,"E12");var subQ1=sQuery(id+"F0.wireOp",EDGE,"E4");var subQ2=makeQuery(id+"F0.imprint","INTERSECT",VERTEX,{"derivedFrom":[subQ1,subQ0]});Q118=makeQuery(id+"F0.imprint","IMPRINT",FACE,{"disambiguationData":[TD([[makeQuery(id+"F0.imprint","IMPRINT",EDGE,{"disambiguationData":[TD([[subQ2,-1.0]])],"derivedFrom":subQ1}),1.0]])]});}
            var Q119;
            {var subQ0=sQuery(id+"F0.wireOp",EDGE,"E10");var subQ1=sQuery(id+"F0.wireOp",EDGE,"E4");var subQ2=makeQuery(id+"F0.imprint","INTERSECT",VERTEX,{"derivedFrom":[subQ1,subQ0]});Q119=makeQuery(id+"F0.imprint","IMPRINT",FACE,{"disambiguationData":[TD([[makeQuery(id+"F0.imprint","IMPRINT",EDGE,{"disambiguationData":[TD([[subQ2,-1.0]])],"derivedFrom":subQ1}),1.0]])]});}
            var Q120;
            {var subQ0=sQuery(id+"F0.wireOp",EDGE,"E160");var subQ1=sQuery(id+"F0.wireOp",EDGE,"E4");var subQ2=makeQuery(id+"F0.imprint","INTERSECT",VERTEX,{"derivedFrom":[subQ1,subQ0]});Q120=makeQuery(id+"F0.imprint","IMPRINT",FACE,{"disambiguationData":[TD([[makeQuery(id+"F0.imprint","IMPRINT",EDGE,{"disambiguationData":[TD([[subQ2,-1.0]])],"derivedFrom":subQ1}),-1.0]])]});}
            var Q121;
            {var subQ0=sQuery(id+"F0.wireOp",EDGE,"E160");var subQ1=sQuery(id+"F0.wireOp",EDGE,"E0.bottom");var subQ2=makeQuery(id+"F0.imprint","INTERSECT",VERTEX,{"derivedFrom":[subQ1,subQ0]});Q121=makeQuery(id+"F0.imprint","IMPRINT",FACE,{"disambiguationData":[TD([[makeQuery(id+"F0.imprint","IMPRINT",EDGE,{"disambiguationData":[TD([[subQ2,-1.0]])],"derivedFrom":subQ1}),-1.0]])]});}
            var Q122;
            {var subQ0=sQuery(id+"F0.wireOp",EDGE,"E160");var subQ1=sQuery(id+"F0.wireOp",EDGE,"E0.top");var subQ2=makeQuery(id+"F0.imprint","INTERSECT",VERTEX,{"derivedFrom":[subQ1,subQ0]});Q122=makeQuery(id+"F0.imprint","IMPRINT",FACE,{"disambiguationData":[TD([[makeQuery(id+"F0.imprint","IMPRINT",EDGE,{"disambiguationData":[TD([[subQ2,-1.0]])],"derivedFrom":subQ1}),1.0]])]});}
            var Q123;
            {var subQ0=sQuery(id+"F0.wireOp",EDGE,"E2");var subQ1=sQuery(id+"F0.wireOp",EDGE,"E0.top");var subQ2=makeQuery(id+"F0.imprint","INTERSECT",VERTEX,{"derivedFrom":[subQ1,subQ0]});Q123=makeQuery(id+"F0.imprint","IMPRINT",FACE,{"disambiguationData":[TD([[makeQuery(id+"F0.imprint","IMPRINT",EDGE,{"disambiguationData":[TD([[subQ2,-1.0]])],"derivedFrom":subQ1}),1.0]])]});}
            var Q124;
            {var subQ0=sQuery(id+"F0.wireOp",EDGE,"E2");var subQ1=sQuery(id+"F0.wireOp",EDGE,"E0.top");var subQ2=makeQuery(id+"F0.imprint","INTERSECT",VERTEX,{"derivedFrom":[subQ1,subQ0]});Q124=makeQuery(id+"F0.imprint","IMPRINT",FACE,{"disambiguationData":[TD([[makeQuery(id+"F0.imprint","IMPRINT",EDGE,{"disambiguationData":[TD([[subQ2,-1.0]])],"derivedFrom":subQ1}),-1.0]])]});}
            var Q125;
            {var subQ0=sQuery(id+"F0.wireOp",EDGE,"E8");var subQ1=sQuery(id+"F0.wireOp",EDGE,"E2");var subQ2=makeQuery(id+"F0.imprint","INTERSECT",VERTEX,{"derivedFrom":[subQ1,subQ0]});Q125=makeQuery(id+"F0.imprint","IMPRINT",FACE,{"disambiguationData":[TD([[makeQuery(id+"F0.imprint","IMPRINT",EDGE,{"disambiguationData":[TD([[subQ2,-1.0]])],"derivedFrom":subQ1}),1.0]])]});}
            var Q126;
            {var subQ0=sQuery(id+"F0.wireOp",EDGE,"E160");var subQ1=sQuery(id+"F0.wireOp",EDGE,"E2");var subQ2=makeQuery(id+"F0.imprint","INTERSECT",VERTEX,{"derivedFrom":[subQ1,subQ0]});Q126=makeQuery(id+"F0.imprint","IMPRINT",FACE,{"disambiguationData":[TD([[makeQuery(id+"F0.imprint","IMPRINT",EDGE,{"disambiguationData":[TD([[subQ2,-1.0]])],"derivedFrom":subQ1}),1.0]])]});}
            var Q127;
            {var subQ0=sQuery(id+"F0.wireOp",EDGE,"E160");var subQ1=sQuery(id+"F0.wireOp",EDGE,"E0.top");var subQ2=makeQuery(id+"F0.imprint","INTERSECT",VERTEX,{"derivedFrom":[subQ1,subQ0]});Q127=makeQuery(id+"F0.imprint","IMPRINT",FACE,{"disambiguationData":[TD([[makeQuery(id+"F0.imprint","IMPRINT",EDGE,{"disambiguationData":[TD([[subQ2,-1.0]])],"derivedFrom":subQ1}),-1.0]])]});}
            var Q128;
            {var subQ0=sQuery(id+"F0.wireOp",EDGE,"E6");var subQ1=sQuery(id+"F0.wireOp",EDGE,"E0.bottom");var subQ2=makeQuery(id+"F0.imprint","INTERSECT",VERTEX,{"derivedFrom":[subQ1,subQ0]});Q128=makeQuery(id+"F0.imprint","IMPRINT",FACE,{"disambiguationData":[TD([[makeQuery(id+"F0.imprint","IMPRINT",EDGE,{"disambiguationData":[TD([[subQ2,-1.0]])],"derivedFrom":subQ1}),1.0]])]});}
            var Q129;
            {var subQ0=sQuery(id+"F0.wireOp",EDGE,"E160");var subQ1=sQuery(id+"F0.wireOp",EDGE,"E2");var subQ2=makeQuery(id+"F0.imprint","INTERSECT",VERTEX,{"derivedFrom":[subQ1,subQ0]});Q129=makeQuery(id+"F0.imprint","IMPRINT",FACE,{"disambiguationData":[TD([[makeQuery(id+"F0.imprint","IMPRINT",EDGE,{"disambiguationData":[TD([[subQ2,-1.0]])],"derivedFrom":subQ1}),-1.0]])]});}
            var Q130;
            {var subQ0=sQuery(id+"F0.wireOp",EDGE,"E10");var subQ1=sQuery(id+"F0.wireOp",EDGE,"E2");var subQ2=makeQuery(id+"F0.imprint","INTERSECT",VERTEX,{"derivedFrom":[subQ1,subQ0]});Q130=makeQuery(id+"F0.imprint","IMPRINT",FACE,{"disambiguationData":[TD([[makeQuery(id+"F0.imprint","IMPRINT",EDGE,{"disambiguationData":[TD([[subQ2,-1.0]])],"derivedFrom":subQ1}),-1.0]])]});}
            var Q131;
            {var subQ0=sQuery(id+"F0.wireOp",EDGE,"E160");var subQ1=sQuery(id+"F0.wireOp",EDGE,"E0.bottom");var subQ2=makeQuery(id+"F0.imprint","INTERSECT",VERTEX,{"derivedFrom":[subQ1,subQ0]});Q131=makeQuery(id+"F0.imprint","IMPRINT",FACE,{"disambiguationData":[TD([[makeQuery(id+"F0.imprint","IMPRINT",EDGE,{"disambiguationData":[TD([[subQ2,-1.0]])],"derivedFrom":subQ1}),1.0]])]});}
            var Q132;
            {var subQ0=sQuery(id+"F0.wireOp",EDGE,"E12");var subQ1=sQuery(id+"F0.wireOp",EDGE,"E0.bottom");var subQ2=makeQuery(id+"F0.imprint","INTERSECT",VERTEX,{"derivedFrom":[subQ1,subQ0]});Q132=makeQuery(id+"F0.imprint","IMPRINT",FACE,{"disambiguationData":[TD([[makeQuery(id+"F0.imprint","IMPRINT",EDGE,{"disambiguationData":[TD([[subQ2,-1.0]])],"derivedFrom":subQ1}),-1.0]])]});}
            var Q133;
            {var subQ0=sQuery(id+"F0.wireOp",EDGE,"E158");var subQ1=sQuery(id+"F0.wireOp",EDGE,"E0.top");var subQ2=makeQuery(id+"F0.imprint","INTERSECT",VERTEX,{"derivedFrom":[subQ1,subQ0]});Q133=makeQuery(id+"F0.imprint","IMPRINT",FACE,{"disambiguationData":[TD([[makeQuery(id+"F0.imprint","IMPRINT",EDGE,{"disambiguationData":[TD([[subQ2,-1.0]])],"derivedFrom":subQ1}),1.0]])]});}
            var Q134;
            {var subQ0=sQuery(id+"F0.wireOp",EDGE,"E4");var subQ1=sQuery(id+"F0.wireOp",EDGE,"E0.top");var subQ2=makeQuery(id+"F0.imprint","INTERSECT",VERTEX,{"derivedFrom":[subQ1,subQ0]});Q134=makeQuery(id+"F0.imprint","IMPRINT",FACE,{"disambiguationData":[TD([[makeQuery(id+"F0.imprint","IMPRINT",EDGE,{"disambiguationData":[TD([[subQ2,-1.0]])],"derivedFrom":subQ1}),-1.0]])]});}
            var Q135;
            {var subQ0=sQuery(id+"F0.wireOp",EDGE,"E158");var subQ1=sQuery(id+"F0.wireOp",EDGE,"E0.top");var subQ2=makeQuery(id+"F0.imprint","INTERSECT",VERTEX,{"derivedFrom":[subQ1,subQ0]});Q135=makeQuery(id+"F0.imprint","IMPRINT",FACE,{"disambiguationData":[TD([[makeQuery(id+"F0.imprint","IMPRINT",EDGE,{"disambiguationData":[TD([[subQ2,-1.0]])],"derivedFrom":subQ1}),-1.0]])]});}
            var Q136;
            {var subQ0=sQuery(id+"F0.wireOp",EDGE,"E12");var subQ1=sQuery(id+"F0.wireOp",EDGE,"E4");var subQ2=makeQuery(id+"F0.imprint","INTERSECT",VERTEX,{"derivedFrom":[subQ1,subQ0]});Q136=makeQuery(id+"F0.imprint","IMPRINT",FACE,{"disambiguationData":[TD([[makeQuery(id+"F0.imprint","IMPRINT",EDGE,{"disambiguationData":[TD([[subQ2,-1.0]])],"derivedFrom":subQ1}),-1.0]])]});}
            var Q137;
            {var subQ0=sQuery(id+"F0.wireOp",EDGE,"E158");var subQ1=sQuery(id+"F0.wireOp",EDGE,"E4");var subQ2=makeQuery(id+"F0.imprint","INTERSECT",VERTEX,{"derivedFrom":[subQ1,subQ0]});Q137=makeQuery(id+"F0.imprint","IMPRINT",FACE,{"disambiguationData":[TD([[makeQuery(id+"F0.imprint","IMPRINT",EDGE,{"disambiguationData":[TD([[subQ2,-1.0]])],"derivedFrom":subQ1}),1.0]])]});}
            var Q138;
            {var subQ0=sQuery(id+"F0.wireOp",EDGE,"E12");var subQ1=sQuery(id+"F0.wireOp",EDGE,"E0.bottom");var subQ2=makeQuery(id+"F0.imprint","INTERSECT",VERTEX,{"derivedFrom":[subQ1,subQ0]});Q138=makeQuery(id+"F0.imprint","IMPRINT",FACE,{"disambiguationData":[TD([[makeQuery(id+"F0.imprint","IMPRINT",EDGE,{"disambiguationData":[TD([[subQ2,-1.0]])],"derivedFrom":subQ1}),1.0]])]});}
            var Q139;
            {var subQ0=sQuery(id+"F0.wireOp",EDGE,"E158");var subQ1=sQuery(id+"F0.wireOp",EDGE,"E0.bottom");var subQ2=makeQuery(id+"F0.imprint","INTERSECT",VERTEX,{"derivedFrom":[subQ1,subQ0]});Q139=makeQuery(id+"F0.imprint","IMPRINT",FACE,{"disambiguationData":[TD([[makeQuery(id+"F0.imprint","IMPRINT",EDGE,{"disambiguationData":[TD([[subQ2,-1.0]])],"derivedFrom":subQ1}),1.0]])]});}
            var Q140;
            {var subQ0=sQuery(id+"F0.wireOp",EDGE,"E158");var subQ1=sQuery(id+"F0.wireOp",EDGE,"E0.bottom");var subQ2=makeQuery(id+"F0.imprint","INTERSECT",VERTEX,{"derivedFrom":[subQ1,subQ0]});Q140=makeQuery(id+"F0.imprint","IMPRINT",FACE,{"disambiguationData":[TD([[makeQuery(id+"F0.imprint","IMPRINT",EDGE,{"disambiguationData":[TD([[subQ2,-1.0]])],"derivedFrom":subQ1}),-1.0]])]});}
            var Q141;
            {var subQ0=sQuery(id+"F0.wireOp",EDGE,"E10");var subQ1=sQuery(id+"F0.wireOp",EDGE,"E0.bottom");var subQ2=makeQuery(id+"F0.imprint","INTERSECT",VERTEX,{"derivedFrom":[subQ1,subQ0]});Q141=makeQuery(id+"F0.imprint","IMPRINT",FACE,{"disambiguationData":[TD([[makeQuery(id+"F0.imprint","IMPRINT",EDGE,{"disambiguationData":[TD([[subQ2,-1.0]])],"derivedFrom":subQ1}),-1.0]])]});}
            var Q142;
            {var subQ0=sQuery(id+"F0.wireOp",EDGE,"E10");var subQ1=sQuery(id+"F0.wireOp",EDGE,"E0.bottom");var subQ2=makeQuery(id+"F0.imprint","INTERSECT",VERTEX,{"derivedFrom":[subQ1,subQ0]});Q142=makeQuery(id+"F0.imprint","IMPRINT",FACE,{"disambiguationData":[TD([[makeQuery(id+"F0.imprint","IMPRINT",EDGE,{"disambiguationData":[TD([[subQ2,-1.0]])],"derivedFrom":subQ1}),1.0]])]});}
            var Q143;
            {var subQ0=sQuery(id+"F0.wireOp",EDGE,"E160");var subQ1=sQuery(id+"F0.wireOp",EDGE,"E10");var subQ2=makeQuery(id+"F0.imprint","INTERSECT",VERTEX,{"derivedFrom":[subQ1,subQ0]});Q143=makeQuery(id+"F0.imprint","IMPRINT",FACE,{"disambiguationData":[TD([[makeQuery(id+"F0.imprint","IMPRINT",EDGE,{"disambiguationData":[TD([[subQ2,-1.0]])],"derivedFrom":subQ1}),1.0]])]});}
            var Q144;
            {var subQ0=sQuery(id+"F0.wireOp",EDGE,"E158");var subQ1=sQuery(id+"F0.wireOp",EDGE,"E12");var subQ2=makeQuery(id+"F0.imprint","INTERSECT",VERTEX,{"derivedFrom":[subQ1,subQ0]});Q144=makeQuery(id+"F0.imprint","IMPRINT",FACE,{"disambiguationData":[TD([[makeQuery(id+"F0.imprint","IMPRINT",EDGE,{"disambiguationData":[TD([[subQ2,-1.0]])],"derivedFrom":subQ1}),1.0]])]});}
            var Q145;
            {var subQ0=sQuery(id+"F0.wireOp",EDGE,"E158");var subQ1=sQuery(id+"F0.wireOp",EDGE,"E4");var subQ2=makeQuery(id+"F0.imprint","INTERSECT",VERTEX,{"derivedFrom":[subQ1,subQ0]});Q145=makeQuery(id+"F0.imprint","IMPRINT",FACE,{"disambiguationData":[TD([[makeQuery(id+"F0.imprint","IMPRINT",EDGE,{"disambiguationData":[TD([[subQ2,-1.0]])],"derivedFrom":subQ1}),-1.0]])]});}
            var Q146;
            {var subQ0=sQuery(id+"F0.wireOp",EDGE,"E6");var subQ1=sQuery(id+"F0.wireOp",EDGE,"E4");var subQ2=makeQuery(id+"F0.imprint","INTERSECT",VERTEX,{"derivedFrom":[subQ1,subQ0]});Q146=makeQuery(id+"F0.imprint","IMPRINT",FACE,{"disambiguationData":[TD([[makeQuery(id+"F0.imprint","IMPRINT",EDGE,{"disambiguationData":[TD([[subQ2,-1.0]])],"derivedFrom":subQ1}),1.0]])]});}
            var Q147;
            {var subQ1=sQuery(id+"F0.wireOp",EDGE,"E146");Q147=makeQuery(id+"F0.imprint","IMPRINT",FACE,{"disambiguationData":[TD([[makeQuery(id+"F0.imprint","IMPRINT",EDGE,{"derivedFrom":subQ1}),1.0]])]});}
            var Q148;
            {var subQ1=sQuery(id+"F0.wireOp",EDGE,"E118");Q148=makeQuery(id+"F0.imprint","IMPRINT",FACE,{"disambiguationData":[TD([[makeQuery(id+"F0.imprint","IMPRINT",EDGE,{"derivedFrom":subQ1}),-1.0]])]});}
            var Q149;
            Q149=makeQuery(id+"F0.imprint","IMPRINT",FACE,{"disambiguationData":[TD([[makeQuery(id+"F0.imprint","IMPRINT",EDGE,{"derivedFrom":sQuery(id+"F0.wireOp",EDGE,"E73")}),1.0]])]});
            extrude(context, id + "F1", {"entities" : qUnion([Q0, Q1, Q2, Q3, Q4, Q5, Q6, Q7, Q8, Q9, Q10, Q11, Q12, Q13, Q14, Q15, Q16, Q17, Q18, Q19, Q20, Q21, Q22, Q23, Q24, Q25, Q26, Q27, Q28, Q29, Q30, Q31, Q32, Q33, Q34, Q35, Q36, Q37, Q38, Q39, Q40, Q41, Q42, Q43, Q44, Q45, Q46, Q47, Q48, Q49, Q50, Q51, Q52, Q53, Q54, Q55, Q56, Q57, Q58, Q59, Q60, Q61, Q62, Q63, Q64, Q65, Q66, Q67, Q68, Q69, Q70, Q71, Q72, Q73, Q74, Q75, Q76, Q77, Q78, Q79, Q80, Q81, Q82, Q83, Q84, Q85, Q86, Q87, Q88, Q89, Q90, Q91, Q92, Q93, Q94, Q95, Q96, Q97, Q98, Q99, Q100, Q101, Q102, Q103, Q104, Q105, Q106, Q107, Q108, Q109, Q110, Q111, Q112, Q113, Q114, Q115, Q116, Q117, Q118, Q119, Q120, Q121, Q122, Q123, Q124, Q125, Q126, Q127, Q128, Q129, Q130, Q131, Q132, Q133, Q134, Q135, Q136, Q137, Q138, Q139, Q140, Q141, Q142, Q143, Q144, Q145, Q146, Q147, Q148, Q149]), "depth" : 5.08 * mm});
        }
    });
